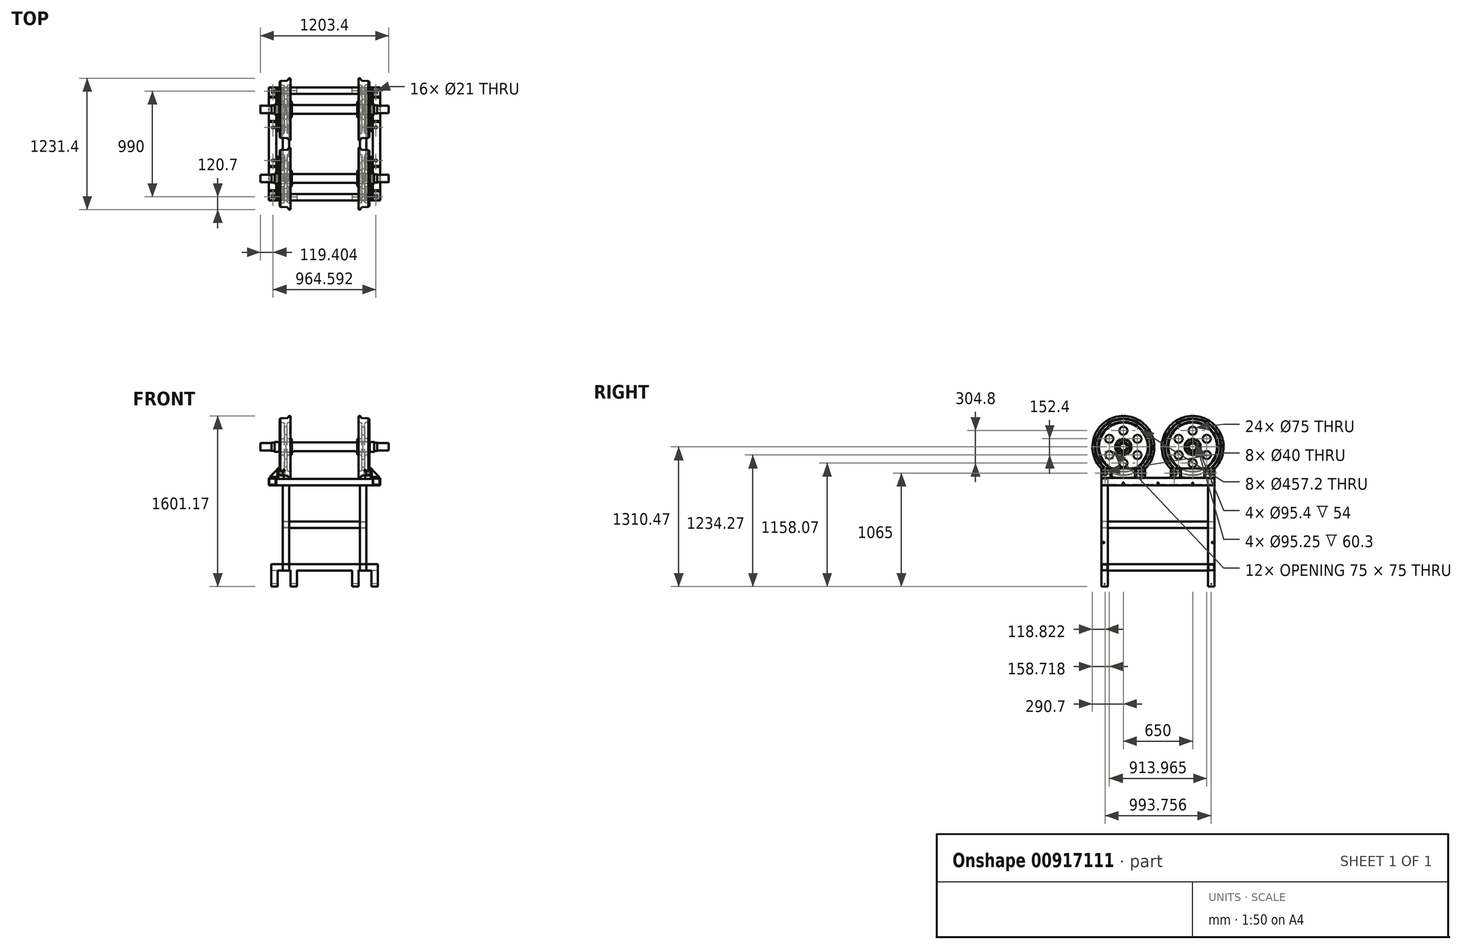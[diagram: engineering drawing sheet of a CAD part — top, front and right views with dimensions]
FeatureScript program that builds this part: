
annotation { "Feature Type Name" : "Feature", "Feature Type Description" : "" }
export const myFeature = defineFeature(function(context is Context, id is Id, definition is map)
    precondition{}
    {
        {
            var Q0;
            Q0=qCreatedBy(makeId("Front.planeOp"),FACE);
            var sketch = newSketch(context, id + "F0", { "sketchPlane" : qUnion([Q0])});
            skLineSegment(sketch, "E0", {"start": v(0, 0) * mm, "end": v(601.65, 0) * mm});
            skLineSegment(sketch, "E1", {"start": v(0, 41.27) * mm, "end": v(285.18, 41.27) * mm});
            skLineSegment(sketch, "E2", {"start": v(0, 41.27) * mm, "end": v(0, 0) * mm});
            skLineSegment(sketch, "E3", {"start": v(306.4, 47.75) * mm, "end": v(360.4, 47.75) * mm});
            skLineSegment(sketch, "E4", {"start": v(306.4, 46.27) * mm, "end": v(306.4, 47.75) * mm});
            skPoint(sketch, "E5.visualSharp", {"position": v(306.4, 41.27) * mm});
            skArc(sketch, "E6", {"start": v(285.18, 41.28) * mm, "mid": v(296.27, 42.93) * mm, "end": v(306.4, 47.75) * mm});
            skLineSegment(sketch, "E7", {"start": v(360.4, 47.69) * mm, "end": v(423.9, 47.69) * mm});
            skLineSegment(sketch, "E8", {"start": v(360.4, 47.69) * mm, "end": v(360.4, 47.75) * mm});
            skLineSegment(sketch, "E9", {"start": v(423.9, 47.69) * mm, "end": v(423.9, 47.5) * mm});
            skLineSegment(sketch, "E10", {"start": v(423.9, 47.5) * mm, "end": v(466.7, 47.5) * mm});
            skLineSegment(sketch, "E11", {"start": v(476.2, 38.1) * mm, "end": v(495.3, 38.1) * mm});
            skLineSegment(sketch, "E12", {"start": v(466.7, 47.6) * mm, "end": v(466.7, 47.5) * mm});
            skPoint(sketch, "E13.visualSharp", {"position": v(466.7, 38.1) * mm});
            skArc(sketch, "E13.filletArc", {"start": v(466.7, 47.6) * mm, "mid": v(469.48, 40.88) * mm, "end": v(476.2, 38.1) * mm});
            skLineSegment(sketch, "E14", {"start": v(502.37, 34.94) * mm, "end": v(601.7, 34.94) * mm});
            skArc(sketch, "E15", {"start": v(502.37, 34.94) * mm, "mid": v(498.5, 35.77) * mm, "end": v(495.3, 38.1) * mm});
            skLineSegment(sketch, "E16", {"start": v(601.7, 34.94) * mm, "end": v(601.65, 0) * mm});
            skLineSegment(sketch, "E17.MirrorCS", {"start": v(-466.7, 47.6) * mm, "end": v(-466.7, 47.5) * mm});
            skLineSegment(sketch, "E18.MirrorCS", {"start": v(-360.4, 47.69) * mm, "end": v(-360.4, 47.75) * mm});
            skLineSegment(sketch, "E19.MirrorCS", {"start": v(-423.9, 47.69) * mm, "end": v(-423.9, 47.5) * mm});
            skLineSegment(sketch, "E20.MirrorCS", {"start": v(-306.4, 46.27) * mm, "end": v(-306.4, 47.75) * mm});
            skArc(sketch, "E21.MirrorCS", {"start": v(-502.37, 34.94) * mm, "mid": v(-498.5, 35.77) * mm, "end": v(-495.3, 38.1) * mm});
            skArc(sketch, "E22.MirrorCS", {"start": v(-466.7, 47.6) * mm, "mid": v(-469.48, 40.88) * mm, "end": v(-476.2, 38.1) * mm});
            skArc(sketch, "E23.MirrorCS", {"start": v(-285.18, 41.28) * mm, "mid": v(-296.27, 42.93) * mm, "end": v(-306.4, 47.75) * mm});
            skLineSegment(sketch, "E24.MirrorCS", {"start": v(-502.37, 34.94) * mm, "end": v(-601.7, 34.94) * mm});
            skLineSegment(sketch, "E25.MirrorCS", {"start": v(-601.7, 34.94) * mm, "end": v(-601.65, 0) * mm});
            skLineSegment(sketch, "E26.MirrorCS", {"start": v(-476.2, 38.1) * mm, "end": v(-495.3, 38.1) * mm});
            skLineSegment(sketch, "E27.MirrorCS", {"start": v(0, 0) * mm, "end": v(-601.65, 0) * mm});
            skLineSegment(sketch, "E28.MirrorCS", {"start": v(-306.4, 47.75) * mm, "end": v(-360.4, 47.75) * mm});
            skLineSegment(sketch, "E29.MirrorCS", {"start": v(-360.4, 47.69) * mm, "end": v(-423.9, 47.69) * mm});
            skLineSegment(sketch, "E30.MirrorCS", {"start": v(-423.9, 47.5) * mm, "end": v(-466.7, 47.5) * mm});
            skPoint(sketch, "E31.MirrorP", {"position": v(-306.4, 41.27) * mm});
            skPoint(sketch, "E32.MirrorP", {"position": v(-466.7, 38.1) * mm});
            skLineSegment(sketch, "E33.MirrorCS", {"start": v(0, 41.27) * mm, "end": v(-285.18, 41.27) * mm});
            skSolve(sketch);
        }
        {
            var Q0;
            Q0=makeQuery(id+"F0.imprint","IMPRINT",FACE,{"disambiguationData":[TD([[makeQuery(id+"F0.imprint","IMPRINT",EDGE,{"derivedFrom":sQuery(id+"F0.wireOp",EDGE,"E2")}),-1.0]])]});
            var Q1;
            Q1=makeQuery(id+"F0.imprint","IMPRINT",FACE,{"disambiguationData":[TD([[makeQuery(id+"F0.imprint","IMPRINT",EDGE,{"derivedFrom":sQuery(id+"F0.wireOp",EDGE,"E0")}),1.0]])]});
            var Q2;
            Q2=sQuery(id+"F0.wireOp",EDGE,"E27.MirrorCS");
            revolve(context, id + "F1", {"surfaceOperationType" : NewSurfaceOperationType.NEW, "entities" : qUnion([Q0, Q1]), "axis" : qUnion([Q2]), "revolveType" : RevolveType.FULL});
        }
        {
            var Q0;
            Q0=makeQuery(id+"F1.opRevolve","SWEPT_EDGE",EDGE,{"disambiguationData":[OSD([sQuery(id+"F0.wireOp",EDGE,"E24.MirrorCS"),sQuery(id+"F0.wireOp",EDGE,"E25.MirrorCS")])]});
            var Q1;
            Q1=makeQuery(id+"F1.opRevolve","SWEPT_EDGE",EDGE,{"disambiguationData":[OSD([sQuery(id+"F0.wireOp",EDGE,"E14"),sQuery(id+"F0.wireOp",EDGE,"E16")])]});
            chamfer(context, id + "F2", {"entities" : qUnion([Q0, Q1]), "width" : 1 * mm, "tangentPropagation" : true});
        }
        {
            var Q0;
            Q0=qCreatedBy(makeId("Front.planeOp"),FACE);
            var sketch = newSketch(context, id + "F3", { "sketchPlane" : qUnion([Q0])});
            skLineSegment(sketch, "E34", {"start": v(0, 0) * mm, "end": v(-306.4, 0) * mm, "construction": true});
            skLineSegment(sketch, "E35", {"start": v(-318.1, 281.2) * mm, "end": v(-318.1, 228.6) * mm});
            skLineSegment(sketch, "E36", {"start": v(-419.7, 266.7) * mm, "end": v(-351.6, 270.27) * mm});
            skLineSegment(sketch, "E37", {"start": v(-327.6, 290.7) * mm, "end": v(-330.1, 290.7) * mm});
            skPoint(sketch, "E38.visualSharp", {"position": v(-318.1, 290.7) * mm});
            skArc(sketch, "E38.filletArc", {"start": v(-318.1, 281.2) * mm, "mid": v(-320.87, 287.92) * mm, "end": v(-327.6, 290.7) * mm});
            skArc(sketch, "E39", {"start": v(-330.1, 290.7) * mm, "mid": v(-337.4, 287.27) * mm, "end": v(-339.43, 279.45) * mm});
            skLineSegment(sketch, "E40", {"start": v(-419.7, 266.7) * mm, "end": v(-419.7, 228.6) * mm});
            skLineSegment(sketch, "E41", {"start": v(-338.9, 284.76) * mm, "end": v(-341.98, 277.13) * mm});
            skArc(sketch, "E42.filletArc", {"start": v(-351.6, 270.27) * mm, "mid": v(-345.8, 272.3) * mm, "end": v(-341.98, 277.13) * mm});
            skLineSegment(sketch, "E43", {"start": v(-306.4, 0) * mm, "end": v(-306.4, 47.7) * mm});
            skLineSegment(sketch, "E44", {"start": v(-306.4, 47.7) * mm, "end": v(-360.4, 47.7) * mm});
            skLineSegment(sketch, "E45", {"start": v(-360.4, 47.7) * mm, "end": v(-360.4, 47.62) * mm});
            skLineSegment(sketch, "E46", {"start": v(-360.4, 47.62) * mm, "end": v(-420.7, 47.62) * mm});
            skLineSegment(sketch, "E47", {"start": v(-306.4, 31) * mm, "end": v(-420.7, 31) * mm, "construction": true});
            skLineSegment(sketch, "E48", {"start": v(-363.55, 31) * mm, "end": v(-363.55, 242.45) * mm, "construction": true});
            skLineSegment(sketch, "E49.0", {"start": v(-352.05, 92.08) * mm, "end": v(-352.05, 212.72) * mm});
            skLineSegment(sketch, "E50.0", {"start": v(-375.05, 92.08) * mm, "end": v(-375.05, 212.72) * mm});
            skLineSegment(sketch, "E51", {"start": v(-419.7, 228.6) * mm, "end": v(-390.93, 228.6) * mm});
            skLineSegment(sketch, "E52", {"start": v(-419.7, 234.95) * mm, "end": v(-413.34, 228.6) * mm});
            skPoint(sketch, "E53.visualSharp", {"position": v(-375.05, 228.6) * mm});
            skArc(sketch, "E53.filletArc", {"start": v(-375.05, 212.72) * mm, "mid": v(-379.7, 223.95) * mm, "end": v(-390.93, 228.6) * mm});
            skLineSegment(sketch, "E54", {"start": v(-390.93, 228.6) * mm, "end": v(-352.05, 228.6) * mm, "construction": true});
            skLineSegment(sketch, "E55", {"start": v(-336.17, 228.6) * mm, "end": v(-318.1, 228.6) * mm});
            skLineSegment(sketch, "E56", {"start": v(-324.44, 228.6) * mm, "end": v(-318.1, 234.95) * mm});
            skArc(sketch, "E57.filletArc", {"start": v(-336.17, 228.6) * mm, "mid": v(-347.4, 223.95) * mm, "end": v(-352.05, 212.72) * mm});
            skLineSegment(sketch, "E58", {"start": v(-420.7, 47.62) * mm, "end": v(-420.7, 0) * mm});
            skLineSegment(sketch, "E59", {"start": v(-420.7, 0) * mm, "end": v(-306.4, 0) * mm});
            skLineSegment(sketch, "E60", {"start": v(-306.4, 76.2) * mm, "end": v(-275.71, 76.2) * mm, "construction": true});
            skLineSegment(sketch, "E61", {"start": v(-306.4, 76.2) * mm, "end": v(-306.4, 47.7) * mm});
            skLineSegment(sketch, "E62", {"start": v(-306.4, 76.2) * mm, "end": v(-336.17, 76.2) * mm});
            skLineSegment(sketch, "E63", {"start": v(-306.4, 69.85) * mm, "end": v(-312.75, 76.2) * mm});
            skArc(sketch, "E64.filletArc", {"start": v(-352.05, 92.08) * mm, "mid": v(-347.4, 80.85) * mm, "end": v(-336.17, 76.2) * mm});
            skLineSegment(sketch, "E65", {"start": v(-390.93, 76.2) * mm, "end": v(-420.7, 76.2) * mm});
            skLineSegment(sketch, "E66", {"start": v(-420.7, 76.2) * mm, "end": v(-420.7, 47.62) * mm});
            skLineSegment(sketch, "E67", {"start": v(-414.35, 76.2) * mm, "end": v(-420.7, 69.85) * mm});
            skPoint(sketch, "E68.newPointB", {"position": v(-375.05, 76.2) * mm});
            skArc(sketch, "E68.filletArc", {"start": v(-390.93, 76.2) * mm, "mid": v(-379.7, 80.85) * mm, "end": v(-375.05, 92.08) * mm});
            skLineSegment(sketch, "E69", {"start": v(-419.7, 260.35) * mm, "end": v(-412.99, 267.05) * mm});
            skSolve(sketch);
        }
        {
            var Q0;
            {var subQ8=sQuery(id+"F3.wireOp",EDGE,"E37");Q0=makeQuery(id+"F3.imprint","IMPRINT",FACE,{"disambiguationData":[TD([[makeQuery(id+"F3.imprint","IMPRINT",EDGE,{"derivedFrom":subQ8}),1.0]])]});}
            var Q1;
            Q1=sQuery(id+"F3.wireOp",EDGE,"E34");
            revolve(context, id + "F4", {"surfaceOperationType" : NewSurfaceOperationType.NEW, "entities" : qUnion([Q0]), "axis" : qUnion([Q1]), "revolveType" : RevolveType.FULL});
        }
        {
            var Q0;
            Q0=makeQuery(id+"F4.opRevolve","SWEPT_FACE",FACE,{"disambiguationData":[OSD([sQuery(id+"F3.wireOp",EDGE,"E50.0")])]});
            var sketch = newSketch(context, id + "F5", { "sketchPlane" : qUnion([Q0])});
            skCircle(sketch, "E70", {"center": v(0, 0) * mm, "radius": 152.4 * mm, "construction": true});
            skLineSegment(sketch, "E71", {"start": v(0, 0) * mm, "end": v(0, 152.4) * mm, "construction": true});
            skCircle(sketch, "E72", {"center": v(0, 152.4) * mm, "radius": 37.5 * mm});
            skCircle(sketch, "E73.1.0", {"center": v(-131.98, 76.2) * mm, "radius": 37.5 * mm});
            skCircle(sketch, "E73.2.0", {"center": v(-131.98, -76.2) * mm, "radius": 37.5 * mm});
            skCircle(sketch, "E73.3.0", {"center": v(0, -152.4) * mm, "radius": 37.5 * mm});
            skCircle(sketch, "E73.4.0", {"center": v(131.98, -76.2) * mm, "radius": 37.5 * mm});
            skCircle(sketch, "E73.5.0", {"center": v(131.98, 76.2) * mm, "radius": 37.5 * mm});
            skSolve(sketch);
        }
        {
            var Q0;
            Q0=makeQuery(id+"F5.imprint","IMPRINT",FACE,{"disambiguationData":[TD([[makeQuery(id+"F5.imprint","IMPRINT",EDGE,{"derivedFrom":sQuery(id+"F5.wireOp",EDGE,"E73.5.0")}),1.0]])]});
            var Q1;
            Q1=makeQuery(id+"F5.imprint","IMPRINT",FACE,{"disambiguationData":[TD([[makeQuery(id+"F5.imprint","IMPRINT",EDGE,{"derivedFrom":sQuery(id+"F5.wireOp",EDGE,"E72")}),1.0]])]});
            var Q2;
            Q2=makeQuery(id+"F5.imprint","IMPRINT",FACE,{"disambiguationData":[TD([[makeQuery(id+"F5.imprint","IMPRINT",EDGE,{"derivedFrom":sQuery(id+"F5.wireOp",EDGE,"E73.1.0")}),1.0]])]});
            var Q3;
            Q3=makeQuery(id+"F5.imprint","IMPRINT",FACE,{"disambiguationData":[TD([[makeQuery(id+"F5.imprint","IMPRINT",EDGE,{"derivedFrom":sQuery(id+"F5.wireOp",EDGE,"E73.2.0")}),1.0]])]});
            var Q4;
            Q4=makeQuery(id+"F5.imprint","IMPRINT",FACE,{"disambiguationData":[TD([[makeQuery(id+"F5.imprint","IMPRINT",EDGE,{"derivedFrom":sQuery(id+"F5.wireOp",EDGE,"E73.4.0")}),1.0]])]});
            var Q5;
            Q5=makeQuery(id+"F5.imprint","IMPRINT",FACE,{"disambiguationData":[TD([[makeQuery(id+"F5.imprint","IMPRINT",EDGE,{"derivedFrom":sQuery(id+"F5.wireOp",EDGE,"E73.3.0")}),1.0]])]});
            extrude(context, id + "F6", {"entities" : qUnion([Q0, Q1, Q2, Q3, Q4, Q5]), "operationType" : NewBodyOperationType.REMOVE, "oppositeDirection" : true, "depth" : 25 * mm, "offsetDistance" : 25 * mm});
        }
        {
            var Q0;
            Q0=makeQuery(id+"F4.opRevolve","SWEPT_BODY",BODY,{"disambiguationData":[OSD([sQuery(id+"F3.wireOp",EDGE,"E35"),sQuery(id+"F3.wireOp",EDGE,"E36"),sQuery(id+"F3.wireOp",EDGE,"E37"),sQuery(id+"F3.wireOp",EDGE,"E38.filletArc"),sQuery(id+"F3.wireOp",EDGE,"E39"),sQuery(id+"F3.wireOp",EDGE,"E40"),sQuery(id+"F3.wireOp",EDGE,"E41"),sQuery(id+"F3.wireOp",EDGE,"E42.filletArc"),sQuery(id+"F3.wireOp",EDGE,"E44"),sQuery(id+"F3.wireOp",EDGE,"E45"),sQuery(id+"F3.wireOp",EDGE,"E46"),sQuery(id+"F3.wireOp",EDGE,"E49.0"),sQuery(id+"F3.wireOp",EDGE,"E50.0"),sQuery(id+"F3.wireOp",EDGE,"E51"),sQuery(id+"F3.wireOp",EDGE,"E52"),sQuery(id+"F3.wireOp",EDGE,"E53.filletArc"),sQuery(id+"F3.wireOp",EDGE,"E55"),sQuery(id+"F3.wireOp",EDGE,"E56"),sQuery(id+"F3.wireOp",EDGE,"E57.filletArc"),sQuery(id+"F3.wireOp",EDGE,"E61"),sQuery(id+"F3.wireOp",EDGE,"E62"),sQuery(id+"F3.wireOp",EDGE,"E63"),sQuery(id+"F3.wireOp",EDGE,"E64.filletArc"),sQuery(id+"F3.wireOp",EDGE,"E65"),sQuery(id+"F3.wireOp",EDGE,"E66"),sQuery(id+"F3.wireOp",EDGE,"E67"),sQuery(id+"F3.wireOp",EDGE,"E68.filletArc"),sQuery(id+"F3.wireOp",EDGE,"E69")])]});
            var Q1;
            Q1=qCreatedBy(makeId("Right.planeOp"),FACE);
            mirror(context, id + "F7", {"entities" : qUnion([Q0]), "mirrorPlane" : qUnion([Q1])});
        }
        {
            var Q0;
            Q0=qCreatedBy(makeId("Front.planeOp"),FACE);
            var sketch = newSketch(context, id + "F8", { "sketchPlane" : qUnion([Q0])});
            skLineSegment(sketch, "E74", {"start": v(0, 0) * mm, "end": v(0, -325.68) * mm, "construction": true});
            skLineSegment(sketch, "E75", {"start": v(412.99, -267.05) * mm, "end": v(351.6, -270.27) * mm});
            skLineSegment(sketch, "E76", {"start": v(382.3, -268.66) * mm, "end": v(382.3, -347.59) * mm, "construction": true});
            skLineSegment(sketch, "E77", {"start": v(0, -325.68) * mm, "end": v(382.3, -325.68) * mm, "construction": true});
            skSolve(sketch);
        }
        {
            var Q0;
            Q0=qCreatedBy(makeId("Right.planeOp"),FACE);
            cPlane(context, id + "F9", {"entities" : qUnion([Q0]), "cplaneType" : CPlaneType.OFFSET, "offset" : 382.3 * mm, "width" : 150 * mm, "height" : 150 * mm});
        }
        {
            var Q0;
            Q0=qCreatedBy(id+"F9.planeOp",FACE);
            var sketch = newSketch(context, id + "F10", { "sketchPlane" : qUnion([Q0])});
            skCircle(sketch, "E78.0", {"center": v(0, 0) * mm, "radius": 267.05 * mm});
            skCircle(sketch, "E79.0", {"center": v(0, 0) * mm, "radius": 270.27 * mm});
            skLineSegment(sketch, "E80", {"start": v(0, 0) * mm, "end": v(0, -364.56) * mm, "construction": true});
            skLineSegment(sketch, "E81", {"start": v(0, 0) * mm, "end": v(-153.17, -218.76) * mm, "construction": true});
            skLineSegment(sketch, "E82", {"start": v(-153.17, -218.76) * mm, "end": v(-155.02, -221.4) * mm, "construction": true});
            skLineSegment(sketch, "E83", {"start": v(-154.1, -220.07) * mm, "end": v(-141.61, -220.07) * mm, "construction": true});
            skLineSegment(sketch, "E84", {"start": v(-155.02, -221.4) * mm, "end": v(-171.88, -245.47) * mm, "construction": true});
            skCircle(sketch, "E85", {"center": v(-171.88, -245.47) * mm, "radius": 31 * mm});
            skCircle(sketch, "E86", {"center": v(-171.88, -245.47) * mm, "radius": 12.5 * mm});
            skCircle(sketch, "E87.MirrorC", {"center": v(171.88, -245.47) * mm, "radius": 31 * mm});
            skCircle(sketch, "E88.MirrorC", {"center": v(171.88, -245.47) * mm, "radius": 12.5 * mm});
            skCircle(sketch, "E89", {"center": v(-171.88, -245.47) * mm, "radius": 20 * mm});
            skCircle(sketch, "E90.MirrorC", {"center": v(171.88, -245.47) * mm, "radius": 20 * mm});
            skCircle(sketch, "E91", {"center": v(-171.88, -245.47) * mm, "radius": 10 * mm});
            skCircle(sketch, "E92.MirrorC", {"center": v(171.88, -245.47) * mm, "radius": 10 * mm});
            skSolve(sketch);
        }
        {
            var Q0;
            Q0=makeQuery(id+"F10.imprint","IMPRINT",FACE,{"disambiguationData":[TD([[makeQuery(id+"F10.imprint","IMPRINT",EDGE,{"derivedFrom":sQuery(id+"F10.wireOp",EDGE,"E86")}),-1.0]])]});
            var Q1;
            Q1=makeQuery(id+"F10.imprint","IMPRINT",FACE,{"disambiguationData":[TD([[makeQuery(id+"F10.imprint","IMPRINT",EDGE,{"derivedFrom":sQuery(id+"F10.wireOp",EDGE,"E88.MirrorC")}),1.0]])]});
            var Q2;
            {var subQ0=sQuery(id+"F10.wireOp",EDGE,"E85");var subQ1=sQuery(id+"F10.wireOp",EDGE,"E79.0");var subQ2=makeQuery(id+"F10.imprint","INTERSECT",VERTEX,{"disambiguationData":[OD(0.0)],"derivedFrom":[subQ1,subQ0]});Q2=makeQuery(id+"F10.imprint","IMPRINT",FACE,{"disambiguationData":[TD([[makeQuery(id+"F10.imprint","IMPRINT",EDGE,{"disambiguationData":[TD([[subQ2,-1.0]])],"derivedFrom":subQ1}),1.0]])]});}
            var Q3;
            {var subQ0=sQuery(id+"F10.wireOp",EDGE,"E87.MirrorC");var subQ1=sQuery(id+"F10.wireOp",EDGE,"E79.0");var subQ2=makeQuery(id+"F10.imprint","INTERSECT",VERTEX,{"disambiguationData":[OD(0.0)],"derivedFrom":[subQ1,subQ0]});Q3=makeQuery(id+"F10.imprint","IMPRINT",FACE,{"disambiguationData":[TD([[makeQuery(id+"F10.imprint","IMPRINT",EDGE,{"disambiguationData":[TD([[subQ2,1.0]])],"derivedFrom":subQ1}),1.0]])]});}
            var Q4;
            Q4=makeQuery(id+"F10.imprint","IMPRINT",FACE,{"disambiguationData":[TD([[makeQuery(id+"F10.imprint","IMPRINT",EDGE,{"derivedFrom":sQuery(id+"F10.wireOp",EDGE,"E89")}),-1.0]])]});
            var Q5;
            Q5=makeQuery(id+"F10.imprint","IMPRINT",FACE,{"disambiguationData":[TD([[makeQuery(id+"F10.imprint","IMPRINT",EDGE,{"derivedFrom":sQuery(id+"F10.wireOp",EDGE,"E90.MirrorC")}),1.0]])]});
            extrude(context, id + "F11", {"entities" : qUnion([Q0, Q1, Q2, Q3, Q4, Q5]), "endBound" : BoundingType.SYMMETRIC, "depth" : 17 * mm, "offsetDistance" : 25 * mm});
        }
        {
            var Q0;
            Q0=makeQuery(id+"F10.imprint","IMPRINT",FACE,{"disambiguationData":[TD([[makeQuery(id+"F10.imprint","IMPRINT",EDGE,{"derivedFrom":sQuery(id+"F10.wireOp",EDGE,"E86")}),-1.0]])]});
            var Q1;
            Q1=makeQuery(id+"F10.imprint","IMPRINT",FACE,{"disambiguationData":[TD([[makeQuery(id+"F10.imprint","IMPRINT",EDGE,{"derivedFrom":sQuery(id+"F10.wireOp",EDGE,"E88.MirrorC")}),1.0]])]});
            var Q2;
            Q2=makeQuery(id+"F10.imprint","IMPRINT",FACE,{"disambiguationData":[TD([[makeQuery(id+"F10.imprint","IMPRINT",EDGE,{"derivedFrom":sQuery(id+"F10.wireOp",EDGE,"E86")}),1.0]])]});
            var Q3;
            Q3=makeQuery(id+"F10.imprint","IMPRINT",FACE,{"disambiguationData":[TD([[makeQuery(id+"F10.imprint","IMPRINT",EDGE,{"derivedFrom":sQuery(id+"F10.wireOp",EDGE,"E88.MirrorC")}),-1.0]])]});
            var Q4;
            Q4=makeQuery(id+"F10.imprint","IMPRINT",FACE,{"disambiguationData":[TD([[makeQuery(id+"F10.imprint","IMPRINT",EDGE,{"derivedFrom":sQuery(id+"F10.wireOp",EDGE,"E92.MirrorC")}),-1.0]])]});
            var Q5;
            Q5=makeQuery(id+"F10.imprint","IMPRINT",FACE,{"disambiguationData":[TD([[makeQuery(id+"F10.imprint","IMPRINT",EDGE,{"derivedFrom":sQuery(id+"F10.wireOp",EDGE,"E91")}),1.0]])]});
            var Q6;
            Q6=makeQuery(id+"F11.opExtrude","CAP_FACE",FACE,{"disambiguationData":[OSD([sQuery(id+"F10.wireOp",EDGE,"E85"),sQuery(id+"F10.wireOp",EDGE,"E86")])],"isStart":false});
            extrude(context, id + "F12", {"entities" : qUnion([Q0, Q1, Q2, Q3, Q4, Q5]), "depth" : 60 * mm, "offsetDistance" : 25 * mm, "hasSecondDirection" : true, "secondDirectionBound" : SecondDirectionBoundingType.UP_TO_SURFACE, "secondDirectionOppositeDirection" : false, "secondDirectionDepth" : 25 * mm, "secondDirectionBoundEntityFace" : qUnion([Q6])});
        }
        {
            var Q0;
            Q0=makeQuery(id+"F10.imprint","IMPRINT",FACE,{"disambiguationData":[TD([[makeQuery(id+"F10.imprint","IMPRINT",EDGE,{"derivedFrom":sQuery(id+"F10.wireOp",EDGE,"E92.MirrorC")}),-1.0]])]});
            var Q1;
            Q1=makeQuery(id+"F10.imprint","IMPRINT",FACE,{"disambiguationData":[TD([[makeQuery(id+"F10.imprint","IMPRINT",EDGE,{"derivedFrom":sQuery(id+"F10.wireOp",EDGE,"E91")}),1.0]])]});
            extrude(context, id + "F13", {"entities" : qUnion([Q0, Q1]), "operationType" : NewBodyOperationType.REMOVE, "depth" : 43 * mm, "offsetDistance" : 25 * mm});
        }
        {
            var Q0;
            Q0=makeQuery(id+"F12.opExtrude","SWEPT_BODY",BODY,{"disambiguationData":[OSD([sQuery(id+"F10.wireOp",EDGE,"E89")])]});
            var Q1;
            Q1=makeQuery(id+"F11.opExtrude","SWEPT_BODY",BODY,{"disambiguationData":[OSD([sQuery(id+"F10.wireOp",EDGE,"E85"),sQuery(id+"F10.wireOp",EDGE,"E86")])]});
            var Q2;
            Q2=makeQuery(id+"F12.opExtrude","SWEPT_BODY",BODY,{"disambiguationData":[OSD([sQuery(id+"F10.wireOp",EDGE,"E90.MirrorC")])]});
            var Q3;
            Q3=makeQuery(id+"F11.opExtrude","SWEPT_BODY",BODY,{"disambiguationData":[OSD([sQuery(id+"F10.wireOp",EDGE,"E87.MirrorC"),sQuery(id+"F10.wireOp",EDGE,"E88.MirrorC")])]});
            var Q4;
            Q4=qCreatedBy(makeId("Right.planeOp"),FACE);
            mirror(context, id + "F14", {"entities" : qUnion([Q0, Q1, Q2, Q3]), "mirrorPlane" : qUnion([Q4])});
        }
        {
            var Q0;
            Q0=makeQuery(id+"F14.opPattern","COPY",FACE,{"derivedFrom":makeQuery(id+"F12.opExtrude","CAP_FACE",FACE,{"disambiguationData":[OSD([sQuery(id+"F10.wireOp",EDGE,"E89")])],"isStart":false}),"instanceName":"1"});
            var sketch = newSketch(context, id + "F15", { "sketchPlane" : qUnion([Q0])});
            skCircle(sketch, "E93.0", {"center": v(171.88, -245.47) * mm, "radius": 20 * mm});
            skCircle(sketch, "E94.0", {"center": v(-171.88, -245.47) * mm, "radius": 20 * mm});
            skLineSegment(sketch, "E95", {"start": v(-171.88, -225.47) * mm, "end": v(-171.88, -200.47) * mm, "construction": true});
            skLineSegment(sketch, "E96", {"start": v(-171.88, -265.47) * mm, "end": v(-171.88, -290.47) * mm, "construction": true});
            skLineSegment(sketch, "E97", {"start": v(-191.88, -245.47) * mm, "end": v(-205, -245.47) * mm, "construction": true});
            skLineSegment(sketch, "E98", {"start": v(-205, -200.47) * mm, "end": v(-205, -290.47) * mm});
            skLineSegment(sketch, "E99", {"start": v(0, 0) * mm, "end": v(0, -330.07) * mm, "construction": true});
            skLineSegment(sketch, "E100", {"start": v(-205, -200.47) * mm, "end": v(0, -200.47) * mm});
            skLineSegment(sketch, "E101", {"start": v(-205, -290.47) * mm, "end": v(0, -290.47) * mm});
            skLineSegment(sketch, "E102.MirrorCS", {"start": v(205, -200.47) * mm, "end": v(0, -200.47) * mm});
            skLineSegment(sketch, "E103.MirrorCS", {"start": v(205, -290.47) * mm, "end": v(0, -290.47) * mm});
            skLineSegment(sketch, "E104.MirrorCS", {"start": v(205, -200.47) * mm, "end": v(205, -290.47) * mm});
            skSolve(sketch);
        }
        {
            var Q0;
            Q0=makeQuery(id+"F15.imprint","IMPRINT",FACE,{"disambiguationData":[TD([[makeQuery(id+"F15.imprint","IMPRINT",EDGE,{"derivedFrom":sQuery(id+"F15.wireOp",EDGE,"E94.0")}),-1.0]])]});
            extrude(context, id + "F16", {"entities" : qUnion([Q0]), "oppositeDirection" : true, "depth" : 10 * mm, "offsetDistance" : 25 * mm});
        }
        {
            var Q0;
            Q0=makeQuery(id+"F16.opExtrude","SWEPT_FACE",FACE,{"disambiguationData":[OSD([sQuery(id+"F15.wireOp",EDGE,"E98")])]});
            var sketch = newSketch(context, id + "F17", { "sketchPlane" : qUnion([Q0])});
            skPoint(sketch, "E105.0", {"position": v(437.3, -290.47) * mm});
            skLineSegment(sketch, "E106.0", {"start": v(432.3, -290.47) * mm, "end": v(442.3, -290.47) * mm});
            skLineSegment(sketch, "E107.0", {"start": v(442.3, -200.47) * mm, "end": v(442.3, -290.47) * mm});
            skLineSegment(sketch, "E108", {"start": v(442.3, -290.47) * mm, "end": v(522.3, -290.47) * mm});
            skLineSegment(sketch, "E109", {"start": v(522.3, -290.47) * mm, "end": v(522.3, -280.47) * mm});
            skLineSegment(sketch, "E110", {"start": v(522.3, -280.47) * mm, "end": v(442.3, -280.47) * mm});
            skLineSegment(sketch, "E111", {"start": v(442.3, -210.47) * mm, "end": v(512.3, -280.47) * mm});
            skSolve(sketch);
        }
        {
            var Q0;
            {var subQ0=sQuery(id+"F17.wireOp",EDGE,"E108");Q0=makeQuery(id+"F17.imprint","IMPRINT",FACE,{"disambiguationData":[TD([[makeQuery(id+"F17.imprint","IMPRINT",EDGE,{"derivedFrom":subQ0}),1.0]])]});}
            var Q1;
            Q1=makeQuery(id+"F16.opExtrude","SWEPT_FACE",FACE,{"disambiguationData":[OSD([sQuery(id+"F15.wireOp",EDGE,"E104.MirrorCS")])]});
            extrude(context, id + "F18", {"entities" : qUnion([Q0]), "operationType" : NewBodyOperationType.ADD, "endBound" : BoundingType.UP_TO_SURFACE, "oppositeDirection" : true, "depth" : 25 * mm, "endBoundEntityFace" : qUnion([Q1]), "offsetDistance" : 25 * mm});
        }
        {
            var Q0;
            {var subQ3=sQuery(id+"F17.wireOp",EDGE,"E111");Q0=makeQuery(id+"F17.imprint","IMPRINT",FACE,{"disambiguationData":[TD([[makeQuery(id+"F17.imprint","IMPRINT",EDGE,{"derivedFrom":subQ3}),-1.0]])]});}
            extrude(context, id + "F19", {"entities" : qUnion([Q0]), "oppositeDirection" : true, "depth" : 95 * mm, "offsetDistance" : 25 * mm, "hasSecondDirection" : true, "secondDirectionOppositeDirection" : true, "secondDirectionDepth" : 85 * mm});
        }
        {
            var Q0;
            Q0=makeQuery(id+"F19.opExtrude","SWEPT_BODY",BODY,{"disambiguationData":[OSD([sQuery(id+"F17.wireOp",EDGE,"E107.0"),sQuery(id+"F17.wireOp",EDGE,"E110"),sQuery(id+"F17.wireOp",EDGE,"E111")])]});
            var Q1;
            Q1=qCreatedBy(makeId("Front.planeOp"),FACE);
            mirror(context, id + "F20", {"entities" : qUnion([Q0]), "mirrorPlane" : qUnion([Q1])});
        }
        {
            var Q0;
            Q0=makeQuery(id+"F18.opExtrude","SWEPT_FACE",FACE,{"disambiguationData":[OSD([sQuery(id+"F17.wireOp",EDGE,"E110")])]});
            var sketch = newSketch(context, id + "F21", { "sketchPlane" : qUnion([Q0])});
            skLineSegment(sketch, "E112.0", {"start": v(-522.3, -205) * mm, "end": v(-522.3, 205) * mm});
            skLineSegment(sketch, "E113.0", {"start": v(-442.3, 205) * mm, "end": v(-512.3, 205) * mm});
            skLineSegment(sketch, "E114.0", {"start": v(-522.3, 205) * mm, "end": v(-442.3, 205) * mm});
            skLineSegment(sketch, "E115", {"start": v(-442.3, 225.61) * mm, "end": v(-522.3, 225.61) * mm, "construction": true});
            skLineSegment(sketch, "E116", {"start": v(-482.3, 225.61) * mm, "end": v(-482.3, 205) * mm, "construction": true});
            skLineSegment(sketch, "E117", {"start": v(-522.3, 0) * mm, "end": v(-482.3, 0) * mm, "construction": true});
            skLineSegment(sketch, "E118", {"start": v(-482.3, 0) * mm, "end": v(-482.3, 170) * mm, "construction": true});
            skLineSegment(sketch, "E119", {"start": v(-482.3, 191.88) * mm, "end": v(-399.3, 191.88) * mm});
            skLineSegment(sketch, "E120", {"start": v(-399.3, 151.88) * mm, "end": v(-482.3, 151.88) * mm});
            skLineSegment(sketch, "E121", {"start": v(-482.3, 170) * mm, "end": v(-502.5, 170) * mm});
            skCircle(sketch, "E122", {"center": v(-482.3, 170) * mm, "radius": 10 * mm});
            skCircle(sketch, "E123.MirrorC", {"center": v(-482.3, -170) * mm, "radius": 10 * mm});
            skSolve(sketch);
        }
        {
            var Q0;
            Q0=makeQuery(id+"F21.imprint","IMPRINT",FACE,{"disambiguationData":[TD([[makeQuery(id+"F21.imprint","IMPRINT",EDGE,{"derivedFrom":sQuery(id+"F21.wireOp",EDGE,"E122")}),1.0]])]});
            var Q1;
            Q1=makeQuery(id+"F21.imprint","IMPRINT",FACE,{"disambiguationData":[TD([[makeQuery(id+"F21.imprint","IMPRINT",EDGE,{"derivedFrom":sQuery(id+"F21.wireOp",EDGE,"E123.MirrorC")}),-1.0]])]});
            extrude(context, id + "F22", {"entities" : qUnion([Q0, Q1]), "operationType" : NewBodyOperationType.REMOVE, "endBound" : BoundingType.THROUGH_ALL, "oppositeDirection" : true, "depth" : 25 * mm, "offsetDistance" : 25 * mm});
        }
        {
            var Q0;
            Q0=makeQuery(id+"F16.opExtrude","SWEPT_BODY",BODY,{"disambiguationData":[OSD([sQuery(id+"F15.wireOp",EDGE,"E94.0"),sQuery(id+"F15.wireOp",EDGE,"E98"),sQuery(id+"F15.wireOp",EDGE,"E100"),sQuery(id+"F15.wireOp",EDGE,"E101"),sQuery(id+"F15.wireOp",EDGE,"E102.MirrorCS"),sQuery(id+"F15.wireOp",EDGE,"E103.MirrorCS"),sQuery(id+"F15.wireOp",EDGE,"E104.MirrorCS"),sQuery(id+"F15.wireOp",EDGE,"E93.0")])]});
            var Q1;
            Q1=makeQuery(id+"F19.opExtrude","SWEPT_BODY",BODY,{"disambiguationData":[OSD([sQuery(id+"F17.wireOp",EDGE,"E107.0"),sQuery(id+"F17.wireOp",EDGE,"E110"),sQuery(id+"F17.wireOp",EDGE,"E111")])]});
            var Q2;
            Q2=makeQuery(id+"F20.opPattern","COPY",BODY,{"derivedFrom":makeQuery(id+"F19.opExtrude","SWEPT_BODY",BODY,{"disambiguationData":[OSD([sQuery(id+"F17.wireOp",EDGE,"E107.0"),sQuery(id+"F17.wireOp",EDGE,"E110"),sQuery(id+"F17.wireOp",EDGE,"E111")])]}),"instanceName":"1"});
            var Q3;
            Q3=makeQuery(id+"F8pm4Jn0m6n4DZo_8.opExtrude","SWEPT_BODY",BODY,{"disambiguationData":[OSD([sQuery(id+"F17.wireOp",EDGE,"E107.0"),sQuery(id+"F17.wireOp",EDGE,"E110"),sQuery(id+"F17.wireOp",EDGE,"E111")])]});
            var Q4;
            Q4=qCreatedBy(makeId("Right.planeOp"),FACE);
            mirror(context, id + "F23", {"entities" : qUnion([Q0, Q1, Q2, Q3]), "mirrorPlane" : qUnion([Q4])});
        }
        {
            var Q0;
            Q0=makeQuery(id+"F23.opPattern","COPY",FACE,{"derivedFrom":makeQuery(id+"F18.opExtrude","SWEPT_FACE",FACE,{"disambiguationData":[OSD([sQuery(id+"F17.wireOp",EDGE,"E109")])]}),"instanceName":"1"});
            var sketch = newSketch(context, id + "F24", { "sketchPlane" : qUnion([Q0])});
            skLineSegment(sketch, "E124.0", {"start": v(-205, -290.47) * mm, "end": v(205, -290.47) * mm});
            skLineSegment(sketch, "E125.0", {"start": v(-180, -280.47) * mm, "end": v(-160, -280.47) * mm});
            skLineSegment(sketch, "E126", {"start": v(-170, -280.47) * mm, "end": v(-170, -290.47) * mm, "construction": true});
            skLineSegment(sketch, "E127", {"start": v(-170, -290.47) * mm, "end": v(-170, -360.47) * mm, "construction": true});
            skLineSegment(sketch, "E128", {"start": v(-170, -360.47) * mm, "end": v(-135, -360.47) * mm});
            skLineSegment(sketch, "E129", {"start": v(-170, -360.47) * mm, "end": v(-205, -360.47) * mm});
            skLineSegment(sketch, "E130", {"start": v(-135, -360.47) * mm, "end": v(-135, -290.47) * mm});
            skLineSegment(sketch, "E131", {"start": v(-205, -360.47) * mm, "end": v(-205, -290.47) * mm});
            skLineSegment(sketch, "E132.0", {"start": v(-140, -355.47) * mm, "end": v(-140, -295.47) * mm});
            skLineSegment(sketch, "E133.0", {"start": v(-200, -355.47) * mm, "end": v(-200, -295.47) * mm});
            skLineSegment(sketch, "E134", {"start": v(-170, -325.47) * mm, "end": v(-161.63, -325.47) * mm, "construction": true});
            skLineSegment(sketch, "E135", {"start": v(-140, -295.47) * mm, "end": v(-200, -295.47) * mm});
            skLineSegment(sketch, "E136.MirrorCS", {"start": v(-140, -355.47) * mm, "end": v(-200, -355.47) * mm});
            skLineSegment(sketch, "E137.MirrorCS", {"start": v(170, -325.47) * mm, "end": v(161.63, -325.47) * mm, "construction": true});
            skLineSegment(sketch, "E138.MirrorCS", {"start": v(140, -355.47) * mm, "end": v(140, -295.47) * mm});
            skLineSegment(sketch, "E139.MirrorCS", {"start": v(205, -360.47) * mm, "end": v(205, -290.47) * mm});
            skLineSegment(sketch, "E140.MirrorCS", {"start": v(140, -355.47) * mm, "end": v(200, -355.47) * mm});
            skLineSegment(sketch, "E141.MirrorCS", {"start": v(170, -360.47) * mm, "end": v(135, -360.47) * mm});
            skLineSegment(sketch, "E142.MirrorCS", {"start": v(170, -290.47) * mm, "end": v(170, -360.47) * mm, "construction": true});
            skLineSegment(sketch, "E143.MirrorCS", {"start": v(170, -360.47) * mm, "end": v(205, -360.47) * mm});
            skLineSegment(sketch, "E144.MirrorCS", {"start": v(135, -360.47) * mm, "end": v(135, -290.47) * mm});
            skLineSegment(sketch, "E145.MirrorCS", {"start": v(200, -355.47) * mm, "end": v(200, -295.47) * mm});
            skLineSegment(sketch, "E146.MirrorCS", {"start": v(140, -295.47) * mm, "end": v(200, -295.47) * mm});
            skSolve(sketch);
        }
        {
            var Q0;
            Q0=makeQuery(id+"F23.opPattern","COPY",FACE,{"derivedFrom":makeQuery(id+"F18.opExtrude","SWEPT_FACE",FACE,{"disambiguationData":[OSD([sQuery(id+"F17.wireOp",EDGE,"E110")])]}),"instanceName":"1"});
            var sketch = newSketch(context, id + "F25", { "sketchPlane" : qUnion([Q0])});
            skCircle(sketch, "E147.0", {"center": v(482.3, -170) * mm, "radius": 10 * mm});
            skCircle(sketch, "E148.0", {"center": v(482.3, 170) * mm, "radius": 10 * mm});
            skCircle(sketch, "E149.0", {"center": v(-482.3, 170) * mm, "radius": 10 * mm});
            skCircle(sketch, "E150.0", {"center": v(-482.3, -170) * mm, "radius": 10 * mm});
            skSolve(sketch);
        }
        {
            var Q0;
            Q0=qCreatedBy(makeId("Front.planeOp"),FACE);
            cPlane(context, id + "F26", {"entities" : qUnion([Q0]), "cplaneType" : CPlaneType.OFFSET, "offset" : 325 * mm, "width" : 150 * mm, "height" : 150 * mm});
        }
        {
            var Q0;
            Q0=makeQuery(id+"F7.opPattern","COPY",BODY,{"derivedFrom":makeQuery(id+"F4.opRevolve","SWEPT_BODY",BODY,{"disambiguationData":[OSD([sQuery(id+"F3.wireOp",EDGE,"E35"),sQuery(id+"F3.wireOp",EDGE,"E36"),sQuery(id+"F3.wireOp",EDGE,"E37"),sQuery(id+"F3.wireOp",EDGE,"E38.filletArc"),sQuery(id+"F3.wireOp",EDGE,"E39"),sQuery(id+"F3.wireOp",EDGE,"E40"),sQuery(id+"F3.wireOp",EDGE,"E41"),sQuery(id+"F3.wireOp",EDGE,"E42.filletArc"),sQuery(id+"F3.wireOp",EDGE,"E44"),sQuery(id+"F3.wireOp",EDGE,"E45"),sQuery(id+"F3.wireOp",EDGE,"E46"),sQuery(id+"F3.wireOp",EDGE,"E49.0"),sQuery(id+"F3.wireOp",EDGE,"E50.0"),sQuery(id+"F3.wireOp",EDGE,"E51"),sQuery(id+"F3.wireOp",EDGE,"E52"),sQuery(id+"F3.wireOp",EDGE,"E53.filletArc"),sQuery(id+"F3.wireOp",EDGE,"E55"),sQuery(id+"F3.wireOp",EDGE,"E56"),sQuery(id+"F3.wireOp",EDGE,"E57.filletArc"),sQuery(id+"F3.wireOp",EDGE,"E61"),sQuery(id+"F3.wireOp",EDGE,"E62"),sQuery(id+"F3.wireOp",EDGE,"E63"),sQuery(id+"F3.wireOp",EDGE,"E64.filletArc"),sQuery(id+"F3.wireOp",EDGE,"E65"),sQuery(id+"F3.wireOp",EDGE,"E66"),sQuery(id+"F3.wireOp",EDGE,"E67"),sQuery(id+"F3.wireOp",EDGE,"E68.filletArc"),sQuery(id+"F3.wireOp",EDGE,"E69")])]}),"instanceName":"1"});
            var Q1;
            Q1=makeQuery(id+"F1.opRevolve","SWEPT_BODY",BODY,{"disambiguationData":[OSD([sQuery(id+"F0.wireOp",EDGE,"E0"),sQuery(id+"F0.wireOp",EDGE,"E1"),sQuery(id+"F0.wireOp",EDGE,"E3"),sQuery(id+"F0.wireOp",EDGE,"E6"),sQuery(id+"F0.wireOp",EDGE,"E7"),sQuery(id+"F0.wireOp",EDGE,"E8"),sQuery(id+"F0.wireOp",EDGE,"E9"),sQuery(id+"F0.wireOp",EDGE,"E10"),sQuery(id+"F0.wireOp",EDGE,"E11"),sQuery(id+"F0.wireOp",EDGE,"E12"),sQuery(id+"F0.wireOp",EDGE,"E13.filletArc"),sQuery(id+"F0.wireOp",EDGE,"E14"),sQuery(id+"F0.wireOp",EDGE,"E15"),sQuery(id+"F0.wireOp",EDGE,"E16"),sQuery(id+"F0.wireOp",EDGE,"E17.MirrorCS"),sQuery(id+"F0.wireOp",EDGE,"E18.MirrorCS"),sQuery(id+"F0.wireOp",EDGE,"E19.MirrorCS"),sQuery(id+"F0.wireOp",EDGE,"E21.MirrorCS"),sQuery(id+"F0.wireOp",EDGE,"E22.MirrorCS"),sQuery(id+"F0.wireOp",EDGE,"E23.MirrorCS"),sQuery(id+"F0.wireOp",EDGE,"E24.MirrorCS"),sQuery(id+"F0.wireOp",EDGE,"E25.MirrorCS"),sQuery(id+"F0.wireOp",EDGE,"E26.MirrorCS"),sQuery(id+"F0.wireOp",EDGE,"E27.MirrorCS"),sQuery(id+"F0.wireOp",EDGE,"E28.MirrorCS"),sQuery(id+"F0.wireOp",EDGE,"E29.MirrorCS"),sQuery(id+"F0.wireOp",EDGE,"E30.MirrorCS"),sQuery(id+"F0.wireOp",EDGE,"E33.MirrorCS")])]});
            var Q2;
            Q2=makeQuery(id+"F4.opRevolve","SWEPT_BODY",BODY,{"disambiguationData":[OSD([sQuery(id+"F3.wireOp",EDGE,"E35"),sQuery(id+"F3.wireOp",EDGE,"E36"),sQuery(id+"F3.wireOp",EDGE,"E37"),sQuery(id+"F3.wireOp",EDGE,"E38.filletArc"),sQuery(id+"F3.wireOp",EDGE,"E39"),sQuery(id+"F3.wireOp",EDGE,"E40"),sQuery(id+"F3.wireOp",EDGE,"E41"),sQuery(id+"F3.wireOp",EDGE,"E42.filletArc"),sQuery(id+"F3.wireOp",EDGE,"E44"),sQuery(id+"F3.wireOp",EDGE,"E45"),sQuery(id+"F3.wireOp",EDGE,"E46"),sQuery(id+"F3.wireOp",EDGE,"E49.0"),sQuery(id+"F3.wireOp",EDGE,"E50.0"),sQuery(id+"F3.wireOp",EDGE,"E51"),sQuery(id+"F3.wireOp",EDGE,"E52"),sQuery(id+"F3.wireOp",EDGE,"E53.filletArc"),sQuery(id+"F3.wireOp",EDGE,"E55"),sQuery(id+"F3.wireOp",EDGE,"E56"),sQuery(id+"F3.wireOp",EDGE,"E57.filletArc"),sQuery(id+"F3.wireOp",EDGE,"E61"),sQuery(id+"F3.wireOp",EDGE,"E62"),sQuery(id+"F3.wireOp",EDGE,"E63"),sQuery(id+"F3.wireOp",EDGE,"E64.filletArc"),sQuery(id+"F3.wireOp",EDGE,"E65"),sQuery(id+"F3.wireOp",EDGE,"E66"),sQuery(id+"F3.wireOp",EDGE,"E67"),sQuery(id+"F3.wireOp",EDGE,"E68.filletArc"),sQuery(id+"F3.wireOp",EDGE,"E69")])]});
            var Q3;
            Q3=makeQuery(id+"F14.opPattern","COPY",BODY,{"derivedFrom":makeQuery(id+"F12.opExtrude","SWEPT_BODY",BODY,{"disambiguationData":[OSD([sQuery(id+"F10.wireOp",EDGE,"E89")])]}),"instanceName":"1"});
            var Q4;
            Q4=makeQuery(id+"F14.opPattern","COPY",BODY,{"derivedFrom":makeQuery(id+"F12.opExtrude","SWEPT_BODY",BODY,{"disambiguationData":[OSD([sQuery(id+"F10.wireOp",EDGE,"E90.MirrorC")])]}),"instanceName":"1"});
            var Q5;
            Q5=makeQuery(id+"FcjCh7YfL3i4wi2_9.opExtrude","SWEPT_BODY",BODY,{"disambiguationData":[OSD([sQuery(id+"F24.wireOp",EDGE,"E124.0"),sQuery(id+"F24.wireOp",EDGE,"E128"),sQuery(id+"F24.wireOp",EDGE,"E129"),sQuery(id+"F24.wireOp",EDGE,"E130"),sQuery(id+"F24.wireOp",EDGE,"E131"),sQuery(id+"F24.wireOp",EDGE,"E132.0"),sQuery(id+"F24.wireOp",EDGE,"E133.0"),sQuery(id+"F24.wireOp",EDGE,"E135"),sQuery(id+"F24.wireOp",EDGE,"E136.MirrorCS")])]});
            var Q6;
            Q6=makeQuery(id+"F8pm4Jn0m6n4DZo_8.opExtrude","SWEPT_BODY",BODY,{"disambiguationData":[OSD([sQuery(id+"F17.wireOp",EDGE,"E107.0"),sQuery(id+"F17.wireOp",EDGE,"E110"),sQuery(id+"F17.wireOp",EDGE,"E111")])]});
            var Q7;
            Q7=makeQuery(id+"F20.opPattern","COPY",BODY,{"derivedFrom":makeQuery(id+"F19.opExtrude","SWEPT_BODY",BODY,{"disambiguationData":[OSD([sQuery(id+"F17.wireOp",EDGE,"E107.0"),sQuery(id+"F17.wireOp",EDGE,"E110"),sQuery(id+"F17.wireOp",EDGE,"E111")])]}),"instanceName":"1"});
            var Q8;
            Q8=makeQuery(id+"F19.opExtrude","SWEPT_BODY",BODY,{"disambiguationData":[OSD([sQuery(id+"F17.wireOp",EDGE,"E107.0"),sQuery(id+"F17.wireOp",EDGE,"E110"),sQuery(id+"F17.wireOp",EDGE,"E111")])]});
            var Q9;
            Q9=makeQuery(id+"F16.opExtrude","SWEPT_BODY",BODY,{"disambiguationData":[OSD([sQuery(id+"F15.wireOp",EDGE,"E94.0"),sQuery(id+"F15.wireOp",EDGE,"E98"),sQuery(id+"F15.wireOp",EDGE,"E100"),sQuery(id+"F15.wireOp",EDGE,"E101"),sQuery(id+"F15.wireOp",EDGE,"E102.MirrorCS"),sQuery(id+"F15.wireOp",EDGE,"E103.MirrorCS"),sQuery(id+"F15.wireOp",EDGE,"E104.MirrorCS"),sQuery(id+"F15.wireOp",EDGE,"E93.0")])]});
            var Q10;
            Q10=makeQuery(id+"FcjCh7YfL3i4wi2_9.opExtrude","SWEPT_BODY",BODY,{"disambiguationData":[OSD([sQuery(id+"F24.wireOp",EDGE,"E124.0"),sQuery(id+"F24.wireOp",EDGE,"E138.MirrorCS"),sQuery(id+"F24.wireOp",EDGE,"E139.MirrorCS"),sQuery(id+"F24.wireOp",EDGE,"E140.MirrorCS"),sQuery(id+"F24.wireOp",EDGE,"E141.MirrorCS"),sQuery(id+"F24.wireOp",EDGE,"E143.MirrorCS"),sQuery(id+"F24.wireOp",EDGE,"E144.MirrorCS"),sQuery(id+"F24.wireOp",EDGE,"E145.MirrorCS"),sQuery(id+"F24.wireOp",EDGE,"E146.MirrorCS")])]});
            var Q11;
            Q11=makeQuery(id+"F12.opExtrude","SWEPT_BODY",BODY,{"disambiguationData":[OSD([sQuery(id+"F10.wireOp",EDGE,"E89")])]});
            var Q12;
            Q12=makeQuery(id+"F12.opExtrude","SWEPT_BODY",BODY,{"disambiguationData":[OSD([sQuery(id+"F10.wireOp",EDGE,"E90.MirrorC")])]});
            var Q13;
            Q13=makeQuery(id+"F14.opPattern","COPY",BODY,{"derivedFrom":makeQuery(id+"F11.opExtrude","SWEPT_BODY",BODY,{"disambiguationData":[OSD([sQuery(id+"F10.wireOp",EDGE,"E87.MirrorC"),sQuery(id+"F10.wireOp",EDGE,"E88.MirrorC")])]}),"instanceName":"1"});
            var Q14;
            Q14=makeQuery(id+"F14.opPattern","COPY",BODY,{"derivedFrom":makeQuery(id+"F11.opExtrude","SWEPT_BODY",BODY,{"disambiguationData":[OSD([sQuery(id+"F10.wireOp",EDGE,"E85"),sQuery(id+"F10.wireOp",EDGE,"E86")])]}),"instanceName":"1"});
            var Q15;
            Q15=makeQuery(id+"F11.opExtrude","SWEPT_BODY",BODY,{"disambiguationData":[OSD([sQuery(id+"F10.wireOp",EDGE,"E85"),sQuery(id+"F10.wireOp",EDGE,"E86")])]});
            var Q16;
            Q16=makeQuery(id+"F11.opExtrude","SWEPT_BODY",BODY,{"disambiguationData":[OSD([sQuery(id+"F10.wireOp",EDGE,"E87.MirrorC"),sQuery(id+"F10.wireOp",EDGE,"E88.MirrorC")])]});
            var Q17;
            Q17=makeQuery(id+"F23.opPattern","COPY",BODY,{"derivedFrom":makeQuery(id+"F16.opExtrude","SWEPT_BODY",BODY,{"disambiguationData":[OSD([sQuery(id+"F15.wireOp",EDGE,"E94.0"),sQuery(id+"F15.wireOp",EDGE,"E98"),sQuery(id+"F15.wireOp",EDGE,"E100"),sQuery(id+"F15.wireOp",EDGE,"E101"),sQuery(id+"F15.wireOp",EDGE,"E102.MirrorCS"),sQuery(id+"F15.wireOp",EDGE,"E103.MirrorCS"),sQuery(id+"F15.wireOp",EDGE,"E104.MirrorCS"),sQuery(id+"F15.wireOp",EDGE,"E93.0")])]}),"instanceName":"1"});
            var Q18;
            Q18=makeQuery(id+"F23.opPattern","COPY",BODY,{"derivedFrom":makeQuery(id+"F8pm4Jn0m6n4DZo_8.opExtrude","SWEPT_BODY",BODY,{"disambiguationData":[OSD([sQuery(id+"F17.wireOp",EDGE,"E107.0"),sQuery(id+"F17.wireOp",EDGE,"E110"),sQuery(id+"F17.wireOp",EDGE,"E111")])]}),"instanceName":"1"});
            var Q19;
            Q19=makeQuery(id+"F23.opPattern","COPY",BODY,{"derivedFrom":makeQuery(id+"F20.opPattern","COPY",BODY,{"derivedFrom":makeQuery(id+"F19.opExtrude","SWEPT_BODY",BODY,{"disambiguationData":[OSD([sQuery(id+"F17.wireOp",EDGE,"E107.0"),sQuery(id+"F17.wireOp",EDGE,"E110"),sQuery(id+"F17.wireOp",EDGE,"E111")])]}),"instanceName":"1"}),"instanceName":"1"});
            var Q20;
            Q20=makeQuery(id+"F23.opPattern","COPY",BODY,{"derivedFrom":makeQuery(id+"F19.opExtrude","SWEPT_BODY",BODY,{"disambiguationData":[OSD([sQuery(id+"F17.wireOp",EDGE,"E107.0"),sQuery(id+"F17.wireOp",EDGE,"E110"),sQuery(id+"F17.wireOp",EDGE,"E111")])]}),"instanceName":"1"});
            var Q21;
            Q21=qCreatedBy(id+"F26.planeOp",FACE);
            mirror(context, id + "F27", {"entities" : qUnion([Q0, Q1, Q2, Q3, Q4, Q5, Q6, Q7, Q8, Q9, Q10, Q11, Q12, Q13, Q14, Q15, Q16, Q17, Q18, Q19, Q20]), "mirrorPlane" : qUnion([Q21])});
        }
        {
            var Q0;
            Q0=makeQuery(id+"F27.opPattern","COPY",FACE,{"derivedFrom":makeQuery(id+"F18.boolean.opBoolean","MERGE",FACE,{"derivedFrom":[makeQuery(id+"F16.opExtrude","SWEPT_FACE",FACE,{"disambiguationData":[OSD([sQuery(id+"F15.wireOp",EDGE,"E98")])]}),makeQuery(id+"F18.opExtrude","CAP_FACE",FACE,{"disambiguationData":[OSD([sQuery(id+"F17.wireOp",EDGE,"E107.0"),sQuery(id+"F17.wireOp",EDGE,"E108"),sQuery(id+"F17.wireOp",EDGE,"E109"),sQuery(id+"F17.wireOp",EDGE,"E110")])],"isStart":true})]}),"instanceName":"1"});
            var sketch = newSketch(context, id + "F28", { "sketchPlane" : qUnion([Q0])});
            skLineSegment(sketch, "E151.0", {"start": v(-442.3, -290.47) * mm, "end": v(-522.3, -290.47) * mm});
            skLineSegment(sketch, "E152", {"start": v(-522.3, -290.47) * mm, "end": v(-522.3, -360.47) * mm});
            skLineSegment(sketch, "E153", {"start": v(-522.3, -360.47) * mm, "end": v(-452.3, -360.47) * mm});
            skLineSegment(sketch, "E154", {"start": v(-452.3, -360.47) * mm, "end": v(-452.3, -290.47) * mm});
            skLineSegment(sketch, "E155.0", {"start": v(-457.3, -355.47) * mm, "end": v(-457.3, -295.47) * mm});
            skLineSegment(sketch, "E156.0", {"start": v(-517.3, -295.47) * mm, "end": v(-517.3, -355.47) * mm});
            skLineSegment(sketch, "E157.0", {"start": v(-517.3, -355.47) * mm, "end": v(-457.3, -355.47) * mm});
            skLineSegment(sketch, "E158.0", {"start": v(-457.3, -295.47) * mm, "end": v(-517.3, -295.47) * mm});
            skLineSegment(sketch, "E159.MirrorCS", {"start": v(452.3, -360.47) * mm, "end": v(452.3, -290.47) * mm});
            skLineSegment(sketch, "E160.MirrorCS", {"start": v(457.3, -295.47) * mm, "end": v(517.3, -295.47) * mm});
            skLineSegment(sketch, "E161.MirrorCS", {"start": v(517.3, -355.47) * mm, "end": v(457.3, -355.47) * mm});
            skLineSegment(sketch, "E162.MirrorCS", {"start": v(522.3, -290.47) * mm, "end": v(522.3, -360.47) * mm});
            skLineSegment(sketch, "E163.MirrorCS", {"start": v(522.3, -360.47) * mm, "end": v(452.3, -360.47) * mm});
            skLineSegment(sketch, "E164.MirrorCS", {"start": v(517.3, -295.47) * mm, "end": v(517.3, -355.47) * mm});
            skLineSegment(sketch, "E165.MirrorCS", {"start": v(457.3, -355.47) * mm, "end": v(457.3, -295.47) * mm});
            skLineSegment(sketch, "E166.0", {"start": v(432.3, -290.47) * mm, "end": v(522.3, -290.47) * mm});
            skSolve(sketch);
        }
        {
            var Q0;
            {var subQ1=sQuery(id+"F28.wireOp",EDGE,"E159.MirrorCS");Q0=makeQuery(id+"F28.imprint","IMPRINT",FACE,{"disambiguationData":[TD([[makeQuery(id+"F28.imprint","IMPRINT",EDGE,{"derivedFrom":subQ1}),-1.0]])]});}
            var Q1;
            {var subQ1=sQuery(id+"F28.wireOp",EDGE,"E152");Q1=makeQuery(id+"F28.imprint","IMPRINT",FACE,{"disambiguationData":[TD([[makeQuery(id+"F28.imprint","IMPRINT",EDGE,{"derivedFrom":subQ1}),1.0]])]});}
            var Q2;
            Q2=makeQuery(id+"F18.boolean.opBoolean","MERGE",FACE,{"derivedFrom":[makeQuery(id+"F16.opExtrude","SWEPT_FACE",FACE,{"disambiguationData":[OSD([sQuery(id+"F15.wireOp",EDGE,"E98")])]}),makeQuery(id+"F18.opExtrude","CAP_FACE",FACE,{"disambiguationData":[OSD([sQuery(id+"F17.wireOp",EDGE,"E107.0"),sQuery(id+"F17.wireOp",EDGE,"E108"),sQuery(id+"F17.wireOp",EDGE,"E109"),sQuery(id+"F17.wireOp",EDGE,"E110")])],"isStart":true})]});
            extrude(context, id + "F29", {"entities" : qUnion([Q0, Q1]), "endBound" : BoundingType.UP_TO_SURFACE, "oppositeDirection" : true, "depth" : 25 * mm, "endBoundEntityFace" : qUnion([Q2]), "offsetDistance" : 25 * mm});
        }
        {
            var Q0;
            Q0=qCreatedBy(makeId("Top.planeOp"),FACE);
            var sketch = newSketch(context, id + "F30", { "sketchPlane" : qUnion([Q0])});
            skCircle(sketch, "E167.0", {"center": v(-482.3, 170) * mm, "radius": 10 * mm});
            skCircle(sketch, "E168.0", {"center": v(-482.3, -170) * mm, "radius": 10 * mm});
            skCircle(sketch, "E169.0", {"center": v(482.3, 170) * mm, "radius": 10 * mm});
            skCircle(sketch, "E170.0", {"center": v(482.3, -170) * mm, "radius": 10 * mm});
            skCircle(sketch, "E171.0", {"center": v(482.3, -480) * mm, "radius": 10 * mm});
            skCircle(sketch, "E172.0", {"center": v(482.3, -820) * mm, "radius": 10 * mm});
            skCircle(sketch, "E173.0", {"center": v(-482.3, -820) * mm, "radius": 10 * mm});
            skCircle(sketch, "E174.0", {"center": v(-482.3, -480) * mm, "radius": 10 * mm});
            skSolve(sketch);
        }
        {
            var Q0;
            Q0=sQuery(id+"F25.wireOp",VERTEX,"E149.0.center");
            var Q1;
            Q1=sQuery(id+"F25.wireOp",VERTEX,"E150.0.center");
            var Q2;
            Q2=sQuery(id+"F25.wireOp",VERTEX,"E148.0.center");
            var Q3;
            Q3=sQuery(id+"F25.wireOp",VERTEX,"E147.0.center");
            var Q4;
            Q4=sQuery(id+"F30.wireOp",VERTEX,"E171.0.center");
            var Q5;
            Q5=sQuery(id+"F30.wireOp",VERTEX,"E172.0.center");
            var Q6;
            Q6=sQuery(id+"F30.wireOp",VERTEX,"E173.0.center");
            var Q7;
            Q7=sQuery(id+"F30.wireOp",VERTEX,"E174.0.center");
            var Q8;
            Q8=makeQuery(id+"F16.opExtrude","SWEPT_BODY",BODY,{"disambiguationData":[OSD([sQuery(id+"F15.wireOp",EDGE,"E94.0"),sQuery(id+"F15.wireOp",EDGE,"E98"),sQuery(id+"F15.wireOp",EDGE,"E100"),sQuery(id+"F15.wireOp",EDGE,"E101"),sQuery(id+"F15.wireOp",EDGE,"E102.MirrorCS"),sQuery(id+"F15.wireOp",EDGE,"E103.MirrorCS"),sQuery(id+"F15.wireOp",EDGE,"E104.MirrorCS"),sQuery(id+"F15.wireOp",EDGE,"E93.0")])]});
            var Q9;
            Q9=makeQuery(id+"F23.opPattern","COPY",BODY,{"derivedFrom":makeQuery(id+"F16.opExtrude","SWEPT_BODY",BODY,{"disambiguationData":[OSD([sQuery(id+"F15.wireOp",EDGE,"E94.0"),sQuery(id+"F15.wireOp",EDGE,"E98"),sQuery(id+"F15.wireOp",EDGE,"E100"),sQuery(id+"F15.wireOp",EDGE,"E101"),sQuery(id+"F15.wireOp",EDGE,"E102.MirrorCS"),sQuery(id+"F15.wireOp",EDGE,"E103.MirrorCS"),sQuery(id+"F15.wireOp",EDGE,"E104.MirrorCS"),sQuery(id+"F15.wireOp",EDGE,"E93.0")])]}),"instanceName":"1"});
            var Q10;
            Q10=makeQuery(id+"F29.opExtrude","SWEPT_BODY",BODY,{"disambiguationData":[OSD([sQuery(id+"F28.wireOp",EDGE,"E151.0"),sQuery(id+"F28.wireOp",EDGE,"E152"),sQuery(id+"F28.wireOp",EDGE,"E153"),sQuery(id+"F28.wireOp",EDGE,"E154"),sQuery(id+"F28.wireOp",EDGE,"E155.0"),sQuery(id+"F28.wireOp",EDGE,"E156.0"),sQuery(id+"F28.wireOp",EDGE,"E157.0"),sQuery(id+"F28.wireOp",EDGE,"E158.0")])]});
            var Q11;
            Q11=makeQuery(id+"F29.opExtrude","SWEPT_BODY",BODY,{"disambiguationData":[OSD([sQuery(id+"F28.wireOp",EDGE,"E159.MirrorCS"),sQuery(id+"F28.wireOp",EDGE,"E160.MirrorCS"),sQuery(id+"F28.wireOp",EDGE,"E161.MirrorCS"),sQuery(id+"F28.wireOp",EDGE,"E162.MirrorCS"),sQuery(id+"F28.wireOp",EDGE,"E163.MirrorCS"),sQuery(id+"F28.wireOp",EDGE,"E164.MirrorCS"),sQuery(id+"F28.wireOp",EDGE,"E165.MirrorCS"),sQuery(id+"F28.wireOp",EDGE,"E166.0")])]});
            var Q12;
            Q12=makeQuery(id+"F27.opPattern","COPY",BODY,{"derivedFrom":makeQuery(id+"F23.opPattern","COPY",BODY,{"derivedFrom":makeQuery(id+"F16.opExtrude","SWEPT_BODY",BODY,{"disambiguationData":[OSD([sQuery(id+"F15.wireOp",EDGE,"E94.0"),sQuery(id+"F15.wireOp",EDGE,"E98"),sQuery(id+"F15.wireOp",EDGE,"E100"),sQuery(id+"F15.wireOp",EDGE,"E101"),sQuery(id+"F15.wireOp",EDGE,"E102.MirrorCS"),sQuery(id+"F15.wireOp",EDGE,"E103.MirrorCS"),sQuery(id+"F15.wireOp",EDGE,"E104.MirrorCS"),sQuery(id+"F15.wireOp",EDGE,"E93.0")])]}),"instanceName":"1"}),"instanceName":"1"});
            var Q13;
            Q13=makeQuery(id+"F27.opPattern","COPY",BODY,{"derivedFrom":makeQuery(id+"F16.opExtrude","SWEPT_BODY",BODY,{"disambiguationData":[OSD([sQuery(id+"F15.wireOp",EDGE,"E94.0"),sQuery(id+"F15.wireOp",EDGE,"E98"),sQuery(id+"F15.wireOp",EDGE,"E100"),sQuery(id+"F15.wireOp",EDGE,"E101"),sQuery(id+"F15.wireOp",EDGE,"E102.MirrorCS"),sQuery(id+"F15.wireOp",EDGE,"E103.MirrorCS"),sQuery(id+"F15.wireOp",EDGE,"E104.MirrorCS"),sQuery(id+"F15.wireOp",EDGE,"E93.0")])]}),"instanceName":"1"});
            hole(context, id + "F31", {"style" : HoleStyle.SIMPLE, "endStyle" : HoleEndStyle.THROUGH, "standardTappedOrClearance" : lookupTablePath({ "standard" : "ISO", "size" : "21", "type" : "Drilled" }), "standardBlindInLast" : lookupTablePath({ "standard" : "ISO", "size" : "21", "type" : "Drilled" }), "holeDiameter" : 21 * mm, "majorDiameter" : 5 * mm, "isTappedThrough" : true, "tappedDepth" : 12 * mm, "tapClearance" : 3, "startFromSketch" : true, "locations" : qUnion([Q0, Q1, Q2, Q3, Q4, Q5, Q6, Q7]), "scope" : qUnion([Q8, Q9, Q10, Q11, Q12, Q13])});
        }
        {
            var Q0;
            Q0=makeQuery(id+"F29.opExtrude","SWEPT_FACE",FACE,{"disambiguationData":[OSD([sQuery(id+"F28.wireOp",EDGE,"E154")])]});
            var sketch = newSketch(context, id + "F32", { "sketchPlane" : qUnion([Q0])});
            skLineSegment(sketch, "E175.0", {"start": v(-855, -360.47) * mm, "end": v(-855, -290.47) * mm});
            skLineSegment(sketch, "E176.0", {"start": v(205, -360.47) * mm, "end": v(-855, -360.47) * mm});
            skLineSegment(sketch, "E177", {"start": v(-855, -300.47) * mm, "end": v(-795, -300.47) * mm});
            skLineSegment(sketch, "E178", {"start": v(-795, -300.47) * mm, "end": v(-795, -360.47) * mm});
            skLineSegment(sketch, "E179.0", {"start": v(-852, -303.47) * mm, "end": v(-798, -303.47) * mm});
            skLineSegment(sketch, "E180.0", {"start": v(-798, -303.47) * mm, "end": v(-798, -357.47) * mm});
            skLineSegment(sketch, "E181.0", {"start": v(-852, -357.47) * mm, "end": v(-852, -303.47) * mm});
            skLineSegment(sketch, "E182.0", {"start": v(-798, -357.47) * mm, "end": v(-852, -357.47) * mm});
            skLineSegment(sketch, "E183.trimOffspring", {"start": v(-852, -300.47) * mm, "end": v(-852, -290.47) * mm});
            skLineSegment(sketch, "E184.MirrorCS", {"start": v(145, -300.47) * mm, "end": v(145, -360.47) * mm});
            skLineSegment(sketch, "E185.MirrorCS", {"start": v(148, -303.47) * mm, "end": v(148, -357.47) * mm});
            skLineSegment(sketch, "E186.MirrorCS", {"start": v(205, -300.47) * mm, "end": v(145, -300.47) * mm});
            skLineSegment(sketch, "E187.MirrorCS", {"start": v(202, -303.47) * mm, "end": v(148, -303.47) * mm});
            skLineSegment(sketch, "E188.MirrorCS", {"start": v(202, -357.47) * mm, "end": v(202, -303.47) * mm});
            skLineSegment(sketch, "E189.MirrorCS", {"start": v(148, -357.47) * mm, "end": v(202, -357.47) * mm});
            skLineSegment(sketch, "E190.0", {"start": v(205, -360.47) * mm, "end": v(205, -290.47) * mm});
            skSolve(sketch);
        }
        {
            var Q0;
            {var subQ1=sQuery(id+"F32.wireOp",EDGE,"E184.MirrorCS");Q0=makeQuery(id+"F32.imprint","IMPRINT",FACE,{"disambiguationData":[TD([[makeQuery(id+"F32.imprint","IMPRINT",EDGE,{"derivedFrom":subQ1}),1.0]])]});}
            var Q1;
            {var subQ0=sQuery(id+"F32.wireOp",EDGE,"E178");Q1=makeQuery(id+"F32.imprint","IMPRINT",FACE,{"disambiguationData":[TD([[makeQuery(id+"F32.imprint","IMPRINT",EDGE,{"derivedFrom":subQ0}),-1.0]])]});}
            var Q2;
            Q2=makeQuery(id+"F29.opExtrude","SWEPT_FACE",FACE,{"disambiguationData":[OSD([sQuery(id+"F28.wireOp",EDGE,"E159.MirrorCS")])]});
            extrude(context, id + "F33", {"entities" : qUnion([Q0, Q1]), "endBound" : BoundingType.UP_TO_SURFACE, "depth" : 25 * mm, "endBoundEntityFace" : qUnion([Q2]), "offsetDistance" : 25 * mm});
        }
        {
            var Q0;
            Q0=makeQuery(id+"F29.opExtrude","SWEPT_FACE",FACE,{"disambiguationData":[OSD([sQuery(id+"F28.wireOp",EDGE,"E163.MirrorCS")])]});
            var sketch = newSketch(context, id + "F34", { "sketchPlane" : qUnion([Q0])});
            skLineSegment(sketch, "E191.MirrorCS", {"start": v(522.3, -70) * mm, "end": v(452.3, -70) * mm});
            skLineSegment(sketch, "E192.0", {"start": v(-522.3, -205) * mm, "end": v(-522.3, 855) * mm});
            skLineSegment(sketch, "E193.0", {"start": v(-452.3, -205) * mm, "end": v(-452.3, 855) * mm});
            skLineSegment(sketch, "E194", {"start": v(0, 0) * mm, "end": v(0, 937.72) * mm, "construction": true});
            skLineSegment(sketch, "E195", {"start": v(342.9, 937.72) * mm, "end": v(342.9, 303.3) * mm, "construction": true});
            skLineSegment(sketch, "E196.0", {"start": v(452.3, 855) * mm, "end": v(-452.3, 855) * mm});
            skLineSegment(sketch, "E197.0", {"start": v(452.3, 795) * mm, "end": v(-452.3, 795) * mm});
            skLineSegment(sketch, "E198.0", {"start": v(452.3, -145) * mm, "end": v(-452.3, -145) * mm});
            skLineSegment(sketch, "E199.0", {"start": v(452.3, -205) * mm, "end": v(-452.3, -205) * mm});
            skLineSegment(sketch, "E200.0", {"start": v(396.9, 937.72) * mm, "end": v(396.9, 303.3) * mm, "construction": true});
            skLineSegment(sketch, "E201.0.0", {"start": v(452.3, -205) * mm, "end": v(522.3, -205) * mm});
            skLineSegment(sketch, "E201.0.1", {"start": v(522.3, -205) * mm, "end": v(522.3, 855) * mm});
            skLineSegment(sketch, "E201.0.2", {"start": v(522.3, 855) * mm, "end": v(452.3, 855) * mm});
            skLineSegment(sketch, "E201.0.3", {"start": v(452.3, 855) * mm, "end": v(452.3, -205) * mm});
            skLineSegment(sketch, "E202", {"start": v(357.9, 855) * mm, "end": v(357.9, 795) * mm, "construction": true});
            skLineSegment(sketch, "E203", {"start": v(340.9, 855) * mm, "end": v(340.9, 795) * mm, "construction": true});
            skLineSegment(sketch, "E204", {"start": v(330.9, 855) * mm, "end": v(330.9, 795) * mm});
            skLineSegment(sketch, "E205", {"start": v(390.9, 855) * mm, "end": v(390.9, 795) * mm});
            skLineSegment(sketch, "E206.0", {"start": v(387.9, 852) * mm, "end": v(387.9, 798) * mm});
            skLineSegment(sketch, "E207.0", {"start": v(333.9, 852) * mm, "end": v(333.9, 798) * mm});
            skLineSegment(sketch, "E208", {"start": v(387.9, 852) * mm, "end": v(333.9, 852) * mm});
            skLineSegment(sketch, "E209", {"start": v(387.9, 798) * mm, "end": v(333.9, 798) * mm});
            skSolve(sketch);
        }
        {
            var Q0;
            {var subQ1=sQuery(id+"F34.wireOp",EDGE,"E204");Q0=makeQuery(id+"F34.imprint","IMPRINT",FACE,{"disambiguationData":[TD([[makeQuery(id+"F34.imprint","IMPRINT",EDGE,{"derivedFrom":subQ1}),1.0]])]});}
            extrude(context, id + "F35", {"entities" : qUnion([Q0]), "depth" : 800 * mm, "offsetDistance" : 25 * mm});
        }
        {
            var Q0;
            Q0=makeQuery(id+"F35.opExtrude","SWEPT_BODY",BODY,{"disambiguationData":[OSD([sQuery(id+"F34.wireOp",EDGE,"E196.0"),sQuery(id+"F34.wireOp",EDGE,"E197.0"),sQuery(id+"F34.wireOp",EDGE,"E204"),sQuery(id+"F34.wireOp",EDGE,"E205"),sQuery(id+"F34.wireOp",EDGE,"E206.0"),sQuery(id+"F34.wireOp",EDGE,"E207.0"),sQuery(id+"F34.wireOp",EDGE,"E208"),sQuery(id+"F34.wireOp",EDGE,"E209")])]});
            var Q1;
            Q1=qCreatedBy(makeId("Right.planeOp"),FACE);
            mirror(context, id + "F36", {"entities" : qUnion([Q0]), "mirrorPlane" : qUnion([Q1])});
        }
        {
            var Q0;
            Q0=makeQuery(id+"F36.opPattern","COPY",BODY,{"derivedFrom":makeQuery(id+"F35.opExtrude","SWEPT_BODY",BODY,{"disambiguationData":[OSD([sQuery(id+"F34.wireOp",EDGE,"E196.0"),sQuery(id+"F34.wireOp",EDGE,"E197.0"),sQuery(id+"F34.wireOp",EDGE,"E204"),sQuery(id+"F34.wireOp",EDGE,"E205"),sQuery(id+"F34.wireOp",EDGE,"E206.0"),sQuery(id+"F34.wireOp",EDGE,"E207.0"),sQuery(id+"F34.wireOp",EDGE,"E208"),sQuery(id+"F34.wireOp",EDGE,"E209")])]}),"instanceName":"1"});
            var Q1;
            Q1=makeQuery(id+"F35.opExtrude","SWEPT_BODY",BODY,{"disambiguationData":[OSD([sQuery(id+"F34.wireOp",EDGE,"E196.0"),sQuery(id+"F34.wireOp",EDGE,"E197.0"),sQuery(id+"F34.wireOp",EDGE,"E204"),sQuery(id+"F34.wireOp",EDGE,"E205"),sQuery(id+"F34.wireOp",EDGE,"E206.0"),sQuery(id+"F34.wireOp",EDGE,"E207.0"),sQuery(id+"F34.wireOp",EDGE,"E208"),sQuery(id+"F34.wireOp",EDGE,"E209")])]});
            var Q2;
            Q2=qCreatedBy(id+"F26.planeOp",FACE);
            mirror(context, id + "F37", {"entities" : qUnion([Q0, Q1]), "mirrorPlane" : qUnion([Q2])});
        }
        {
            var Q0;
            Q0=makeQuery(id+"F35.opExtrude","SWEPT_FACE",FACE,{"disambiguationData":[OSD([sQuery(id+"F34.wireOp",EDGE,"E196.0")])]});
            var sketch = newSketch(context, id + "F38", { "sketchPlane" : qUnion([Q0])});
            skLineSegment(sketch, "E210.0", {"start": v(390.9, -1160.47) * mm, "end": v(330.9, -1160.47) * mm});
            skLineSegment(sketch, "E211", {"start": v(390.9, -1160.47) * mm, "end": v(420.9, -1160.47) * mm});
            skLineSegment(sketch, "E212", {"start": v(330.9, -1160.47) * mm, "end": v(330.9, -1250.47) * mm});
            skLineSegment(sketch, "E213.0", {"start": v(340.9, -1170.47) * mm, "end": v(340.9, -1250.47) * mm});
            skLineSegment(sketch, "E214.0", {"start": v(420.9, -1170.47) * mm, "end": v(340.9, -1170.47) * mm});
            skLineSegment(sketch, "E215", {"start": v(420.9, -1170.47) * mm, "end": v(420.9, -1160.47) * mm});
            skLineSegment(sketch, "E216", {"start": v(340.9, -1250.47) * mm, "end": v(330.9, -1250.47) * mm});
            skSolve(sketch);
        }
        {
            var Q0;
            Q0=makeQuery(id+"F37.opPattern","COPY",FACE,{"derivedFrom":makeQuery(id+"F35.opExtrude","SWEPT_FACE",FACE,{"disambiguationData":[OSD([sQuery(id+"F34.wireOp",EDGE,"E204")])]}),"instanceName":"1"});
            var sketch = newSketch(context, id + "F39", { "sketchPlane" : qUnion([Q0])});
            skLineSegment(sketch, "E217.0", {"start": v(-205, -1160.47) * mm, "end": v(-145, -1160.47) * mm});
            skLineSegment(sketch, "E218.0", {"start": v(-205, -1100.47) * mm, "end": v(-145, -1100.47) * mm});
            skLineSegment(sketch, "E219", {"start": v(-145, -1100.47) * mm, "end": v(-145, -1160.47) * mm});
            skLineSegment(sketch, "E220", {"start": v(-205, -1100.47) * mm, "end": v(-205, -1160.47) * mm});
            skLineSegment(sketch, "E221.0", {"start": v(-202, -1103.47) * mm, "end": v(-148, -1103.47) * mm});
            skLineSegment(sketch, "E222.0", {"start": v(-202, -1157.47) * mm, "end": v(-148, -1157.47) * mm});
            skLineSegment(sketch, "E223.0", {"start": v(-202, -1103.47) * mm, "end": v(-202, -1157.47) * mm});
            skLineSegment(sketch, "E224.0", {"start": v(-148, -1103.47) * mm, "end": v(-148, -1157.47) * mm});
            skSolve(sketch);
        }
        {
            var Q0;
            Q0=makeQuery(id+"F39.imprint","IMPRINT",FACE,{"disambiguationData":[TD([[makeQuery(id+"F39.imprint","IMPRINT",EDGE,{"derivedFrom":sQuery(id+"F39.wireOp",EDGE,"E217.0")}),1.0]])]});
            var Q1;
            Q1=makeQuery(id+"F37.opPattern","COPY",FACE,{"derivedFrom":makeQuery(id+"F36.opPattern","COPY",FACE,{"derivedFrom":makeQuery(id+"F35.opExtrude","SWEPT_FACE",FACE,{"disambiguationData":[OSD([sQuery(id+"F34.wireOp",EDGE,"E204")])]}),"instanceName":"1"}),"instanceName":"1"});
            var Q2;
            Q2=makeQuery(id+"F37.opPattern","COPY",FACE,{"derivedFrom":makeQuery(id+"F35.opExtrude","SWEPT_FACE",FACE,{"disambiguationData":[OSD([sQuery(id+"F34.wireOp",EDGE,"E205")])]}),"instanceName":"1"});
            extrude(context, id + "F40", {"entities" : qUnion([Q0]), "endBound" : BoundingType.UP_TO_SURFACE, "depth" : 25 * mm, "endBoundEntityFace" : qUnion([Q1]), "hasOffset" : true, "offsetDistance" : 120 * mm + 48.44 * mm, "offsetOppositeDirection" : true, "hasSecondDirection" : true, "secondDirectionBound" : SecondDirectionBoundingType.UP_TO_SURFACE, "secondDirectionOppositeDirection" : true, "secondDirectionDepth" : 25 * mm, "secondDirectionBoundEntityFace" : qUnion([Q2]), "hasSecondDirectionOffset" : true, "secondDirectionOffsetDistance" : 60 * mm + 48.44 * mm, "secondDirectionOffsetOppositeDirection" : true});
        }
        {
            var Q0;
            Q0=makeQuery(id+"F37.opPattern","COPY",FACE,{"derivedFrom":makeQuery(id+"F36.opPattern","COPY",FACE,{"derivedFrom":makeQuery(id+"F35.opExtrude","SWEPT_FACE",FACE,{"disambiguationData":[OSD([sQuery(id+"F34.wireOp",EDGE,"E197.0")])]}),"instanceName":"1"}),"instanceName":"1"});
            var sketch = newSketch(context, id + "F41", { "sketchPlane" : qUnion([Q0])});
            skLineSegment(sketch, "E225.0", {"start": v(-390.9, -1160.47) * mm, "end": v(-330.9, -1160.47) * mm});
            skLineSegment(sketch, "E226.0", {"start": v(-390.9, -1100.47) * mm, "end": v(-330.9, -1100.47) * mm});
            skLineSegment(sketch, "E227", {"start": v(-330.9, -1100.47) * mm, "end": v(-330.9, -1160.47) * mm});
            skLineSegment(sketch, "E228", {"start": v(-390.9, -1100.47) * mm, "end": v(-390.9, -1160.47) * mm});
            skLineSegment(sketch, "E229.0", {"start": v(-387.9, -1103.47) * mm, "end": v(-333.9, -1103.47) * mm});
            skLineSegment(sketch, "E230.0", {"start": v(-387.9, -1103.47) * mm, "end": v(-387.9, -1157.47) * mm});
            skLineSegment(sketch, "E231.0", {"start": v(-333.9, -1103.47) * mm, "end": v(-333.9, -1157.47) * mm});
            skLineSegment(sketch, "E232.0", {"start": v(-387.9, -1157.47) * mm, "end": v(-333.9, -1157.47) * mm});
            skSolve(sketch);
        }
        {
            var Q0;
            Q0=makeQuery(id+"F41.imprint","IMPRINT",FACE,{"disambiguationData":[TD([[makeQuery(id+"F41.imprint","IMPRINT",EDGE,{"derivedFrom":sQuery(id+"F41.wireOp",EDGE,"E225.0")}),1.0]])]});
            var Q1;
            Q1=makeQuery(id+"F36.opPattern","COPY",FACE,{"derivedFrom":makeQuery(id+"F35.opExtrude","SWEPT_FACE",FACE,{"disambiguationData":[OSD([sQuery(id+"F34.wireOp",EDGE,"E197.0")])]}),"instanceName":"1"});
            extrude(context, id + "F42", {"entities" : qUnion([Q0]), "endBound" : BoundingType.UP_TO_SURFACE, "depth" : 25 * mm, "endBoundEntityFace" : qUnion([Q1]), "offsetDistance" : 25 * mm});
        }
        {
            var Q0;
            Q0=makeQuery(id+"F42.opExtrude","SWEPT_BODY",BODY,{"disambiguationData":[OSD([sQuery(id+"F41.wireOp",EDGE,"E225.0"),sQuery(id+"F41.wireOp",EDGE,"E226.0"),sQuery(id+"F41.wireOp",EDGE,"E227"),sQuery(id+"F41.wireOp",EDGE,"E228"),sQuery(id+"F41.wireOp",EDGE,"E229.0"),sQuery(id+"F41.wireOp",EDGE,"E230.0"),sQuery(id+"F41.wireOp",EDGE,"E231.0"),sQuery(id+"F41.wireOp",EDGE,"E232.0")])]});
            var Q1;
            Q1=qCreatedBy(makeId("Right.planeOp"),FACE);
            mirror(context, id + "F43", {"entities" : qUnion([Q0]), "mirrorPlane" : qUnion([Q1])});
        }
        {
            var Q0;
            Q0=makeQuery(id+"F40.opExtrude","SWEPT_BODY",BODY,{"disambiguationData":[OSD([sQuery(id+"F39.wireOp",EDGE,"E217.0"),sQuery(id+"F39.wireOp",EDGE,"E218.0"),sQuery(id+"F39.wireOp",EDGE,"E219"),sQuery(id+"F39.wireOp",EDGE,"E220"),sQuery(id+"F39.wireOp",EDGE,"E221.0"),sQuery(id+"F39.wireOp",EDGE,"E222.0"),sQuery(id+"F39.wireOp",EDGE,"E223.0"),sQuery(id+"F39.wireOp",EDGE,"E224.0")])]});
            var Q1;
            Q1=qCreatedBy(id+"F26.planeOp",FACE);
            mirror(context, id + "F44", {"entities" : qUnion([Q0]), "mirrorPlane" : qUnion([Q1])});
        }
        {
            var Q0;
            Q0=makeQuery(id+"F42.opExtrude","SWEPT_FACE",FACE,{"disambiguationData":[OSD([sQuery(id+"F41.wireOp",EDGE,"E226.0")])]});
            cPlane(context, id + "F45", {"entities" : qUnion([Q0]), "cplaneType" : CPlaneType.OFFSET, "offset" : 170 * mm, "width" : 150 * mm, "height" : 150 * mm});
        }
        {
            var Q0;
            Q0=makeQuery(id+"F40.opExtrude","SWEPT_FACE",FACE,{"disambiguationData":[OSD([sQuery(id+"F39.wireOp",EDGE,"E220")])]});
            var sketch = newSketch(context, id + "F46", { "sketchPlane" : qUnion([Q0])});
            skLineSegment(sketch, "E233", {"start": v(0, -1160.47) * mm, "end": v(0, -1341) * mm, "construction": true});
            skLineSegment(sketch, "E234", {"start": v(342.9, -1160.47) * mm, "end": v(342.9, -1286.26) * mm, "construction": true});
            skLineSegment(sketch, "E235", {"start": v(393.7, -1160.47) * mm, "end": v(393.7, -1278.74) * mm, "construction": true});
            skLineSegment(sketch, "E236", {"start": v(319.96, -1160.47) * mm, "end": v(319.96, -1310.47) * mm});
            skLineSegment(sketch, "E237.0", {"start": v(259.96, -1160.47) * mm, "end": v(259.96, -1310.47) * mm});
            skLineSegment(sketch, "E238", {"start": v(319.96, -1310.47) * mm, "end": v(259.96, -1310.47) * mm});
            skLineSegment(sketch, "E239", {"start": v(499.34, -1160.47) * mm, "end": v(499.34, -1310.47) * mm});
            skLineSegment(sketch, "E240.0", {"start": v(439.34, -1160.47) * mm, "end": v(439.34, -1310.47) * mm});
            skLineSegment(sketch, "E241", {"start": v(439.34, -1310.47) * mm, "end": v(499.34, -1310.47) * mm});
            skLineSegment(sketch, "E242.MirrorCS", {"start": v(-259.96, -1160.47) * mm, "end": v(-259.96, -1310.47) * mm});
            skLineSegment(sketch, "E243.MirrorCS", {"start": v(-319.96, -1160.47) * mm, "end": v(-319.96, -1310.47) * mm});
            skLineSegment(sketch, "E244.MirrorCS", {"start": v(-319.96, -1310.47) * mm, "end": v(-259.96, -1310.47) * mm});
            skLineSegment(sketch, "E245.MirrorCS", {"start": v(-439.34, -1160.47) * mm, "end": v(-439.34, -1310.47) * mm});
            skLineSegment(sketch, "E246.MirrorCS", {"start": v(-499.34, -1160.47) * mm, "end": v(-499.34, -1310.47) * mm});
            skLineSegment(sketch, "E247.MirrorCS", {"start": v(-439.34, -1310.47) * mm, "end": v(-499.34, -1310.47) * mm});
            skSolve(sketch);
        }
        {
            var Q0;
            {var subQ0=sQuery(id+"F46.wireOp",EDGE,"E245.MirrorCS");Q0=makeQuery(id+"F46.imprint","IMPRINT",FACE,{"disambiguationData":[TD([[makeQuery(id+"F46.imprint","IMPRINT",EDGE,{"derivedFrom":subQ0}),-1.0]])]});}
            var Q1;
            {var subQ0=sQuery(id+"F46.wireOp",EDGE,"E242.MirrorCS");Q1=makeQuery(id+"F46.imprint","IMPRINT",FACE,{"disambiguationData":[TD([[makeQuery(id+"F46.imprint","IMPRINT",EDGE,{"derivedFrom":subQ0}),-1.0]])]});}
            var Q2;
            {var subQ0=sQuery(id+"F46.wireOp",EDGE,"E236");Q2=makeQuery(id+"F46.imprint","IMPRINT",FACE,{"disambiguationData":[TD([[makeQuery(id+"F46.imprint","IMPRINT",EDGE,{"derivedFrom":subQ0}),-1.0]])]});}
            var Q3;
            {var subQ0=sQuery(id+"F46.wireOp",EDGE,"E239");Q3=makeQuery(id+"F46.imprint","IMPRINT",FACE,{"disambiguationData":[TD([[makeQuery(id+"F46.imprint","IMPRINT",EDGE,{"derivedFrom":subQ0}),-1.0]])]});}
            extrude(context, id + "F47", {"entities" : qUnion([Q0, Q1, Q2, Q3]), "oppositeDirection" : true, "depth" : 60 * mm, "offsetDistance" : 25.4 * mm});
        }
        {
            var Q0;
            Q0=makeQuery(id+"F47.opExtrude","SWEPT_FACE",FACE,{"disambiguationData":[OSD([sQuery(id+"F46.wireOp",EDGE,"E239")])]});
            var sketch = newSketch(context, id + "F48", { "sketchPlane" : qUnion([Q0])});
            skLineSegment(sketch, "E248", {"start": v(-175, -1310.47) * mm, "end": v(-175, -1285.47) * mm, "construction": true});
            skPoint(sketch, "E249", {"position": v(-175, -1285.47) * mm});
            skSolve(sketch);
        }
        {
            var Q0;
            Q0=sQuery(id+"F48.wireOp",VERTEX,"E249");
            var Q1;
            Q1=makeQuery(id+"F47.opExtrude","SWEPT_BODY",BODY,{"disambiguationData":[OSD([sQuery(id+"F39.wireOp",EDGE,"E217.0"),sQuery(id+"F39.wireOp",EDGE,"E220"),sQuery(id+"F46.wireOp",EDGE,"E236"),sQuery(id+"F46.wireOp",EDGE,"E237.0"),sQuery(id+"F46.wireOp",EDGE,"E238")])]});
            var Q2;
            Q2=makeQuery(id+"F47.opExtrude","SWEPT_BODY",BODY,{"disambiguationData":[OSD([sQuery(id+"F39.wireOp",EDGE,"E217.0"),sQuery(id+"F39.wireOp",EDGE,"E220"),sQuery(id+"F46.wireOp",EDGE,"E239"),sQuery(id+"F46.wireOp",EDGE,"E240.0"),sQuery(id+"F46.wireOp",EDGE,"E241")])]});
            var Q3;
            Q3=makeQuery(id+"F47.opExtrude","SWEPT_BODY",BODY,{"disambiguationData":[OSD([sQuery(id+"F39.wireOp",EDGE,"E217.0"),sQuery(id+"F39.wireOp",EDGE,"E220"),sQuery(id+"F46.wireOp",EDGE,"E242.MirrorCS"),sQuery(id+"F46.wireOp",EDGE,"E243.MirrorCS"),sQuery(id+"F46.wireOp",EDGE,"E244.MirrorCS")])]});
            var Q4;
            Q4=makeQuery(id+"F47.opExtrude","SWEPT_BODY",BODY,{"disambiguationData":[OSD([sQuery(id+"F39.wireOp",EDGE,"E217.0"),sQuery(id+"F39.wireOp",EDGE,"E220"),sQuery(id+"F46.wireOp",EDGE,"E245.MirrorCS"),sQuery(id+"F46.wireOp",EDGE,"E246.MirrorCS"),sQuery(id+"F46.wireOp",EDGE,"E247.MirrorCS")])]});
            hole(context, id + "F49", {"style" : HoleStyle.SIMPLE, "endStyle" : HoleEndStyle.THROUGH, "standardTappedOrClearance" : lookupTablePath({ "standard" : "ANSI", "size" : "1/2 (0.5)", "type" : "Drilled" }), "standardBlindInLast" : lookupTablePath({ "standard" : "ANSI", "size" : "1/2 (0.5)", "type" : "Drilled" }), "holeDiameter" : 1 / 50.8 * mm, "majorDiameter" : 6.35 * mm, "isTappedThrough" : true, "tappedDepth" : 12.7 * mm, "tapClearance" : 3, "startFromSketch" : true, "locations" : qUnion([Q0]), "scope" : qUnion([Q1, Q2, Q3, Q4])});
        }
        {
            var Q0;
            Q0=makeQuery(id+"F47.opExtrude","SWEPT_BODY",BODY,{"disambiguationData":[OSD([sQuery(id+"F39.wireOp",EDGE,"E217.0"),sQuery(id+"F39.wireOp",EDGE,"E220"),sQuery(id+"F46.wireOp",EDGE,"E242.MirrorCS"),sQuery(id+"F46.wireOp",EDGE,"E243.MirrorCS"),sQuery(id+"F46.wireOp",EDGE,"E244.MirrorCS")])]});
            var Q1;
            Q1=makeQuery(id+"F47.opExtrude","SWEPT_BODY",BODY,{"disambiguationData":[OSD([sQuery(id+"F39.wireOp",EDGE,"E217.0"),sQuery(id+"F39.wireOp",EDGE,"E220"),sQuery(id+"F46.wireOp",EDGE,"E245.MirrorCS"),sQuery(id+"F46.wireOp",EDGE,"E246.MirrorCS"),sQuery(id+"F46.wireOp",EDGE,"E247.MirrorCS")])]});
            var Q2;
            Q2=makeQuery(id+"F47.opExtrude","SWEPT_BODY",BODY,{"disambiguationData":[OSD([sQuery(id+"F39.wireOp",EDGE,"E217.0"),sQuery(id+"F39.wireOp",EDGE,"E220"),sQuery(id+"F46.wireOp",EDGE,"E236"),sQuery(id+"F46.wireOp",EDGE,"E237.0"),sQuery(id+"F46.wireOp",EDGE,"E238")])]});
            var Q3;
            Q3=makeQuery(id+"F47.opExtrude","SWEPT_BODY",BODY,{"disambiguationData":[OSD([sQuery(id+"F39.wireOp",EDGE,"E217.0"),sQuery(id+"F39.wireOp",EDGE,"E220"),sQuery(id+"F46.wireOp",EDGE,"E239"),sQuery(id+"F46.wireOp",EDGE,"E240.0"),sQuery(id+"F46.wireOp",EDGE,"E241")])]});
            var Q4;
            Q4=qCreatedBy(id+"F26.planeOp",FACE);
            mirror(context, id + "F50", {"operationType" : NewBodyOperationType.ADD, "entities" : qUnion([Q0, Q1, Q2, Q3]), "mirrorPlane" : qUnion([Q4])});
        }
        {
            var Q0;
            Q0=makeQuery(id+"F37.opPattern","COPY",FACE,{"derivedFrom":makeQuery(id+"F36.opPattern","COPY",FACE,{"derivedFrom":makeQuery(id+"F35.opExtrude","SWEPT_FACE",FACE,{"disambiguationData":[OSD([sQuery(id+"F34.wireOp",EDGE,"E204")])]}),"instanceName":"1"}),"instanceName":"1"});
            var sketch = newSketch(context, id + "F51", { "sketchPlane" : qUnion([Q0])});
            skPoint(sketch, "E250.0", {"position": v(145, -1100.47) * mm});
            skLineSegment(sketch, "E251", {"start": v(145, -1100.47) * mm, "end": v(145, -760.47) * mm, "construction": true});
            skLineSegment(sketch, "E252.0", {"start": v(145, -1160.47) * mm, "end": v(145, -360.47) * mm});
            skLineSegment(sketch, "E253.0", {"start": v(205, -1160.47) * mm, "end": v(205, -360.47) * mm});
            skLineSegment(sketch, "E254.bottom", {"start": v(145, -760.47) * mm, "end": v(205, -760.47) * mm});
            skLineSegment(sketch, "E254.top", {"start": v(145, -700.47) * mm, "end": v(205, -700.47) * mm});
            skLineSegment(sketch, "E254.left", {"start": v(145, -760.47) * mm, "end": v(145, -700.47) * mm});
            skLineSegment(sketch, "E254.right", {"start": v(205, -760.47) * mm, "end": v(205, -700.47) * mm});
            skSolve(sketch);
        }
        {
            var Q0;
            Q0=makeQuery(id+"F51.imprint","IMPRINT",FACE,{"disambiguationData":[TD([[makeQuery(id+"F51.imprint","IMPRINT",EDGE,{"derivedFrom":sQuery(id+"F51.wireOp",EDGE,"E254.bottom")}),1.0]])]});
            var Q1;
            Q1=makeQuery(id+"F37.opPattern","COPY",FACE,{"derivedFrom":makeQuery(id+"F35.opExtrude","SWEPT_FACE",FACE,{"disambiguationData":[OSD([sQuery(id+"F34.wireOp",EDGE,"E204")])]}),"instanceName":"1"});
            extrude(context, id + "F52", {"entities" : qUnion([Q0]), "endBound" : BoundingType.UP_TO_SURFACE, "depth" : 25 * mm, "endBoundEntityFace" : qUnion([Q1]), "offsetDistance" : 25 * mm});
        }
        {
            var Q0;
            Q0=makeQuery(id+"F52.opExtrude","SWEPT_BODY",BODY,{"disambiguationData":[OSD([sQuery(id+"F51.wireOp",EDGE,"E254.bottom"),sQuery(id+"F51.wireOp",EDGE,"E254.top"),sQuery(id+"F51.wireOp",EDGE,"E254.left"),sQuery(id+"F51.wireOp",EDGE,"E254.right")])]});
            var Q1;
            Q1=qCreatedBy(id+"F26.planeOp",FACE);
            mirror(context, id + "F53", {"entities" : qUnion([Q0]), "mirrorPlane" : qUnion([Q1])});
        }
        {
            var Q0;
            Q0=makeQuery(id+"F42.opExtrude","SWEPT_BODY",BODY,{"disambiguationData":[OSD([sQuery(id+"F41.wireOp",EDGE,"E225.0"),sQuery(id+"F41.wireOp",EDGE,"E226.0"),sQuery(id+"F41.wireOp",EDGE,"E227"),sQuery(id+"F41.wireOp",EDGE,"E228"),sQuery(id+"F41.wireOp",EDGE,"E229.0"),sQuery(id+"F41.wireOp",EDGE,"E230.0"),sQuery(id+"F41.wireOp",EDGE,"E231.0"),sQuery(id+"F41.wireOp",EDGE,"E232.0")])]});
            var Q1;
            Q1=makeQuery(id+"F43.opPattern","COPY",BODY,{"derivedFrom":makeQuery(id+"F42.opExtrude","SWEPT_BODY",BODY,{"disambiguationData":[OSD([sQuery(id+"F41.wireOp",EDGE,"E225.0"),sQuery(id+"F41.wireOp",EDGE,"E226.0"),sQuery(id+"F41.wireOp",EDGE,"E227"),sQuery(id+"F41.wireOp",EDGE,"E228"),sQuery(id+"F41.wireOp",EDGE,"E229.0"),sQuery(id+"F41.wireOp",EDGE,"E230.0"),sQuery(id+"F41.wireOp",EDGE,"E231.0"),sQuery(id+"F41.wireOp",EDGE,"E232.0")])]}),"instanceName":"1"});
            var Q2;
            Q2=qCreatedBy(id+"F45.planeOp",FACE);
            mirror(context, id + "F54", {"entities" : qUnion([Q0, Q1]), "mirrorPlane" : qUnion([Q2])});
        }
        {
            var Q0;
            Q0=makeQuery(id+"F29.opExtrude","SWEPT_FACE",FACE,{"disambiguationData":[OSD([sQuery(id+"F28.wireOp",EDGE,"E162.MirrorCS")])]});
            var sketch = newSketch(context, id + "F55", { "sketchPlane" : qUnion([Q0])});
            skLineSegment(sketch, "E255.0.0", {"start": v(205, -360.47) * mm, "end": v(205, -290.47) * mm});
            skLineSegment(sketch, "E255.0.1", {"start": v(205, -290.47) * mm, "end": v(-855, -290.47) * mm});
            skLineSegment(sketch, "E255.0.2", {"start": v(-855, -290.47) * mm, "end": v(-855, -360.47) * mm});
            skLineSegment(sketch, "E255.0.3", {"start": v(-855, -360.47) * mm, "end": v(205, -360.47) * mm});
            skLineSegment(sketch, "E256", {"start": v(-855, -340.47) * mm, "end": v(205, -340.47) * mm, "construction": true});
            skLineSegment(sketch, "E257", {"start": v(-325, -340.47) * mm, "end": v(-325, -395.95) * mm, "construction": true});
            skLineSegment(sketch, "E258", {"start": v(0, -340.47) * mm, "end": v(0, -393.02) * mm, "construction": true});
            skLineSegment(sketch, "E259.MirrorCS", {"start": v(-650, -340.47) * mm, "end": v(-650, -393.02) * mm, "construction": true});
            skSolve(sketch);
        }
        {
            var Q0;
            Q0=sQuery(id+"F55.wireOp",VERTEX,"E259.MirrorCS.start");
            var Q1;
            Q1=sQuery(id+"F55.wireOp",VERTEX,"E257.start");
            var Q2;
            Q2=sQuery(id+"F55.wireOp",VERTEX,"E258.start");
            var Q3;
            Q3=makeQuery(id+"F29.opExtrude","SWEPT_BODY",BODY,{"disambiguationData":[OSD([sQuery(id+"F28.wireOp",EDGE,"E151.0"),sQuery(id+"F28.wireOp",EDGE,"E152"),sQuery(id+"F28.wireOp",EDGE,"E153"),sQuery(id+"F28.wireOp",EDGE,"E154"),sQuery(id+"F28.wireOp",EDGE,"E155.0"),sQuery(id+"F28.wireOp",EDGE,"E156.0"),sQuery(id+"F28.wireOp",EDGE,"E157.0"),sQuery(id+"F28.wireOp",EDGE,"E158.0")])]});
            var Q4;
            Q4=makeQuery(id+"F29.opExtrude","SWEPT_BODY",BODY,{"disambiguationData":[OSD([sQuery(id+"F28.wireOp",EDGE,"E159.MirrorCS"),sQuery(id+"F28.wireOp",EDGE,"E160.MirrorCS"),sQuery(id+"F28.wireOp",EDGE,"E161.MirrorCS"),sQuery(id+"F28.wireOp",EDGE,"E162.MirrorCS"),sQuery(id+"F28.wireOp",EDGE,"E163.MirrorCS"),sQuery(id+"F28.wireOp",EDGE,"E164.MirrorCS"),sQuery(id+"F28.wireOp",EDGE,"E165.MirrorCS"),sQuery(id+"F28.wireOp",EDGE,"E166.0")])]});
            hole(context, id + "F56", {"style" : HoleStyle.SIMPLE, "endStyle" : HoleEndStyle.THROUGH, "standardTappedOrClearance" : lookupTablePath({ "standard" : "ISO", "size" : "12", "type" : "Drilled" }), "standardBlindInLast" : lookupTablePath({ "standard" : "ISO", "size" : "12", "type" : "Drilled" }), "holeDiameter" : 12 * mm, "majorDiameter" : 5 * mm, "isTappedThrough" : true, "tappedDepth" : 12 * mm, "tapClearance" : 3, "startFromSketch" : true, "locations" : qUnion([Q0, Q1, Q2]), "scope" : qUnion([Q3, Q4])});
        }
        {
            var Q0;
            Q0=makeQuery(id+"F35.opExtrude","SWEPT_FACE",FACE,{"disambiguationData":[OSD([sQuery(id+"F34.wireOp",EDGE,"E205")])]});
            var sketch = newSketch(context, id + "F57", { "sketchPlane" : qUnion([Q0])});
            skLineSegment(sketch, "E260", {"start": v(-835, -360.47) * mm, "end": v(-835, -896.96) * mm, "construction": true});
            skLineSegment(sketch, "E261.MirrorCS", {"start": v(185, -360.47) * mm, "end": v(185, -896.96) * mm, "construction": true});
            skSolve(sketch);
        }
        {
            var Q0;
            Q0=sQuery(id+"F57.wireOp",VERTEX,"E260.end");
            var Q1;
            Q1=sQuery(id+"F57.wireOp",VERTEX,"E261.MirrorCS.end");
            var Q2;
            Q2=makeQuery(id+"F35.opExtrude","SWEPT_BODY",BODY,{"disambiguationData":[OSD([sQuery(id+"F34.wireOp",EDGE,"E196.0"),sQuery(id+"F34.wireOp",EDGE,"E197.0"),sQuery(id+"F34.wireOp",EDGE,"E204"),sQuery(id+"F34.wireOp",EDGE,"E205"),sQuery(id+"F34.wireOp",EDGE,"E206.0"),sQuery(id+"F34.wireOp",EDGE,"E207.0"),sQuery(id+"F34.wireOp",EDGE,"E208"),sQuery(id+"F34.wireOp",EDGE,"E209")])]});
            var Q3;
            Q3=makeQuery(id+"F36.opPattern","COPY",BODY,{"derivedFrom":makeQuery(id+"F35.opExtrude","SWEPT_BODY",BODY,{"disambiguationData":[OSD([sQuery(id+"F34.wireOp",EDGE,"E196.0"),sQuery(id+"F34.wireOp",EDGE,"E197.0"),sQuery(id+"F34.wireOp",EDGE,"E204"),sQuery(id+"F34.wireOp",EDGE,"E205"),sQuery(id+"F34.wireOp",EDGE,"E206.0"),sQuery(id+"F34.wireOp",EDGE,"E207.0"),sQuery(id+"F34.wireOp",EDGE,"E208"),sQuery(id+"F34.wireOp",EDGE,"E209")])]}),"instanceName":"1"});
            var Q4;
            Q4=makeQuery(id+"F37.opPattern","COPY",BODY,{"derivedFrom":makeQuery(id+"F35.opExtrude","SWEPT_BODY",BODY,{"disambiguationData":[OSD([sQuery(id+"F34.wireOp",EDGE,"E196.0"),sQuery(id+"F34.wireOp",EDGE,"E197.0"),sQuery(id+"F34.wireOp",EDGE,"E204"),sQuery(id+"F34.wireOp",EDGE,"E205"),sQuery(id+"F34.wireOp",EDGE,"E206.0"),sQuery(id+"F34.wireOp",EDGE,"E207.0"),sQuery(id+"F34.wireOp",EDGE,"E208"),sQuery(id+"F34.wireOp",EDGE,"E209")])]}),"instanceName":"1"});
            var Q5;
            Q5=makeQuery(id+"F37.opPattern","COPY",BODY,{"derivedFrom":makeQuery(id+"F36.opPattern","COPY",BODY,{"derivedFrom":makeQuery(id+"F35.opExtrude","SWEPT_BODY",BODY,{"disambiguationData":[OSD([sQuery(id+"F34.wireOp",EDGE,"E196.0"),sQuery(id+"F34.wireOp",EDGE,"E197.0"),sQuery(id+"F34.wireOp",EDGE,"E204"),sQuery(id+"F34.wireOp",EDGE,"E205"),sQuery(id+"F34.wireOp",EDGE,"E206.0"),sQuery(id+"F34.wireOp",EDGE,"E207.0"),sQuery(id+"F34.wireOp",EDGE,"E208"),sQuery(id+"F34.wireOp",EDGE,"E209")])]}),"instanceName":"1"}),"instanceName":"1"});
            hole(context, id + "F58", {"style" : HoleStyle.SIMPLE, "endStyle" : HoleEndStyle.THROUGH, "standardTappedOrClearance" : lookupTablePath({ "standard" : "ISO", "size" : "12", "type" : "Drilled" }), "standardBlindInLast" : lookupTablePath({ "standard" : "ISO", "size" : "12", "type" : "Drilled" }), "holeDiameter" : 12 * mm, "majorDiameter" : 5 * mm, "isTappedThrough" : true, "tappedDepth" : 12 * mm, "tapClearance" : 3, "startFromSketch" : true, "locations" : qUnion([Q0, Q1]), "scope" : qUnion([Q2, Q3, Q4, Q5])});
        }
    });
